FCSTD DOCUMENT  (FreeCAD 1.0R39319 (Git))
Label: ASSEMBLY-TEK2-PCB
License: All rights reserved
LicenseURL: https://en.wikipedia.org/wiki/All_rights_reserved
objects: App::Link×21, Part::FeaturePython×7, App::DocumentObjectGroup×3, PartDesign::CoordinateSystem×1, App::FeaturePython×1, App::Part×1
note: 8 computed .brp shape members not serialized (recipe doc carries the construction recipe); baked Part::Feature solids carry a one-line shape summary decoded from their .brp
EXTERNAL_REF file=PCBAs/PCBA-VSNX.FCStd obj=LCS_1
EXTERNAL_REF file=PCBAs/PCBA-VSNX.FCStd obj=PCBA_VSNX_3D_1
EXTERNAL_REF file=PCBAs/PCBA-VSNX.FCStd obj=Plane_2
EXTERNAL_REF file=PCBAs/PCBA-VSNX-SPACER.FCStd obj=Plane_Bottom_1
EXTERNAL_REF file=PCBAs/PCBA-VSNX-SPACER.FCStd obj=PCBA_VSNX_SPACER_3D_1
EXTERNAL_REF file=PCBAs/PCBA-VSNX-SPACER.FCStd obj=Plane_Top_1
EXTERNAL_REF file=PCBAs/PCBA-VSNX-LCDMOUNT-LEFT.FCStd obj=Plane_1
EXTERNAL_REF file=PCBAs/PCBA-VSNX-LCDMOUNT-TEK2.FCStd obj=PCBA_VSNX_LCDMOUNT_3D_1
EXTERNAL_REF file=PCBAs/PCBA-VSNX.FCStd obj=Axis_3
EXTERNAL_REF file=../Design/THT-ENDLESSPOT/THT-ENDLESSPOT.FCStd obj=Axis_1
EXTERNAL_REF file=../Design/THT-ENDLESSPOT/THT-ENDLESSPOT.FCStd obj=Body
EXTERNAL_REF file=PCBAs/PCBA-VSNX-LCDMOUNT-LEFT.FCStd obj=CircleAxis_1
EXTERNAL_REF file=../Design/SCREW-M1.6x5-C/SCREW-M1.6x5-C.FCStd obj=CircleAxis_1
EXTERNAL_REF file=../Design/SCREW-M1.6x5-C/SCREW-M1.6x5-C.FCStd obj=Body
EXTERNAL_REF file=PCBAs/PCBA-VSNX-LCDMOUNT-LEFT.FCStd obj=CircleAxis_2
EXTERNAL_REF file=PCBAs/PCBA-VSNX-LCDMOUNT-LEFT.FCStd obj=CircleAxis_3
EXTERNAL_REF file=PCBAs/PCBA-VSNX-LCDMOUNT-LEFT.FCStd obj=CircleAxis_4
EXTERNAL_REF file=PCBAs/PCBA-VSNX-LCDMOUNT-LEFT.FCStd obj=CircleAxis_5
EXTERNAL_REF file=PCBAs/PCBA-VSNX-LCDMOUNT-LEFT.FCStd obj=CircleAxis_6
EXTERNAL_REF file=PCBAs/PCBA-VSNX-LCDMOUNT-LEFT.FCStd obj=CircleAxis_7
EXTERNAL_REF file=PCBAs/PCBA-VSNX-LCDMOUNT-LEFT.FCStd obj=CircleAxis_8
EXTERNAL_REF file=PCBAs/PCBA-VSNX-LCDMOUNT-LEFT.FCStd obj=LCS_2
EXTERNAL_REF file=../Design/THT-HALL-SWITCH/THT-HALL-SWITCH.FCStd obj=LCS_Origin
EXTERNAL_REF file=../Design/THT-HALL-SWITCH/THT-HALL-SWITCH.FCStd obj=Body
EXTERNAL_REF file=../Design/PLASTIC-LOW-PROFILE-KEYCAP/PLASTIC-LOW-PROFILE-KEYCAP_THT.FCStd obj=LCS_1
EXTERNAL_REF file=../Design/THT-HALL-SWITCH/THT-HALL-SWITCH.FCStd obj=LCS_1
EXTERNAL_REF file=../Design/PLASTIC-LOW-PROFILE-KEYCAP/PLASTIC-LOW-PROFILE-KEYCAP_THT.FCStd obj=Body
EXTERNAL_REF file=PCBAs/PCBA-VSNX.FCStd obj=LCS_3
EXTERNAL_REF file=../Design/SPACER/SPACER.FCStd obj=LCS_1
EXTERNAL_REF file=../Design/SPACER/SPACER.FCStd obj=Body004
EXTERNAL_REF file=PCBAs/PCBA-VSNX.FCStd obj=LCS_4
EXTERNAL_REF file=../Design/SCREW-M1.6x8/SCREW-M1.6x8.FCStd obj=LCS_1
EXTERNAL_REF file=../Design/SPACER/SPACER.FCStd obj=LCS_2
EXTERNAL_REF file=../Design/SCREW-M1.6x8/SCREW-M1.6x8.FCStd obj=Body
EXTERNAL_REF file=../Design/PLASTIC-TEK2-KNOB-INTERFACE/PLASTIC-TEK2-KNOB-INTERFACE.FCStd obj=LCS_2
EXTERNAL_REF file=../Design/THT-ENDLESSPOT/THT-ENDLESSPOT.FCStd obj=LCS_2
EXTERNAL_REF file=../Design/PLASTIC-TEK2-KNOB-INTERFACE/PLASTIC-TEK2-KNOB-INTERFACE.FCStd obj=Body
EXTERNAL_REF file=../Design/KNOB-TEK2/KNOB-TEK2.FCStd obj=LCS_1
EXTERNAL_REF file=../Design/PLASTIC-TEK2-KNOB-INTERFACE/PLASTIC-TEK2-KNOB-INTERFACE.FCStd obj=LCS_1
EXTERNAL_REF file=../Design/KNOB-TEK2/KNOB-TEK2.FCStd obj=Body

FEATURE [App::DocumentObjectGroup] Parts
FEATURE [PartDesign::CoordinateSystem] LCS_Origin
  AttacherType = Attacher::AttachEngine3D
  AttachmentSupport = -> [X_Axis]
  MapMode = 2
FEATURE [App::DocumentObjectGroup] Constraints
FEATURE [App::FeaturePython] Variables  # WARN: FeaturePython — macro-defined, semantics opaque (R4)
  Type = App::PropertyContainer
FEATURE [App::DocumentObjectGroup] Configurations
FEATURE [App::Link] PCBA_VSNX_3D_1  label="PCBA-VSNX-3D 1"
  AttachedBy = #LCS_1
  AttachedTo = Parent Assembly#LCS_Origin
  LinkedObject = -> <external PCBAs/PCBA-VSNX.FCStd>#PCBA_VSNX_3D_1
  SolverId = Asm4EE
  expr: Placement = LCS_Origin.Placement * AttachmentOffset * PCBA_VSNX#LCS_1.Placement ^ -1
FEATURE [App::Link] PCBA_VSNX_SPACER_3D_1  label="PCBA-VSNX-SPACER-3D 1"
  AttachedBy = #Plane_Bottom_1
  AttachedTo = PCBA_VSNX_3D_1#Plane_2
  AttachmentOffset = pos=(0,0,0) rot=(1,0,0;3.14159rad)
  LinkPlacement = pos=(0,0,1.51) rot=(0,0,1;0rad)
  LinkedObject = -> <external PCBAs/PCBA-VSNX-SPACER.FCStd>#PCBA_VSNX_SPACER_3D_1
  Placement = pos=(0,0,1.51) rot=(0,0,1;0rad)
  SolverId = Asm4EE
  expr: Placement = PCBA_VSNX_3D_1.Placement * PCBA_VSNX#Plane_2.Placement * AttachmentOffset * PCBA_VSNX_SPACER#Plane_Bottom_1.Placement ^ -1
FEATURE [App::Link] PCBA_VSNX_SPACER_3D_002  label="PCBA-VSNX-SPACER-3D 002"
  AttachedBy = #Plane_Bottom_1
  AttachedTo = PCBA_VSNX_SPACER_3D_1#Plane_Top_1
  AttachmentOffset = pos=(0,0,0) rot=(1,0,0;3.14159rad)
  LinkPlacement = pos=(0,0,2.62) rot=(0,0,1;0rad)
  LinkedObject = -> <external PCBAs/PCBA-VSNX-SPACER.FCStd>#PCBA_VSNX_SPACER_3D_1
  Placement = pos=(0,0,2.62) rot=(0,0,1;0rad)
  SolverId = Asm4EE
  expr: Placement = PCBA_VSNX_SPACER_3D_1.Placement * PCBA_VSNX_SPACER#Plane_Top_1.Placement * AttachmentOffset * PCBA_VSNX_SPACER#Plane_Bottom_1.Placement ^ -1
FEATURE [App::Link] PCBA_VSNX_LCDMOUNT_3D_1  label="PCBA-VSNX-LCDMOUNT-3D 1"
  AttachedBy = #Plane_1
  AttachedTo = PCBA_VSNX_SPACER_3D_002#Plane_Top_1
  AttachmentOffset = pos=(0,0,0) rot=(1,0,0;3.14159rad)
  LinkPlacement = pos=(0,0,3.73) rot=(0,0,1;0rad)
  LinkedObject = -> <external PCBAs/PCBA-VSNX-LCDMOUNT-TEK2.FCStd>#PCBA_VSNX_LCDMOUNT_3D_1
  Placement = pos=(0,0,3.73) rot=(0,0,1;0rad)
  SolverId = Asm4EE
  expr: Placement = PCBA_VSNX_SPACER_3D_002.Placement * PCBA_VSNX_SPACER#Plane_Top_1.Placement * AttachmentOffset * PCBA_VSNX_LCDMOUNT_LEFT#Plane_1.Placement ^ -1
FEATURE [App::Link] THT_ENDLESSPOT  label="THT-ENDLESSPOT"
  AttachedBy = #Axis_1
  AttachedTo = PCBA_VSNX_3D_1#Axis_3
  AttachmentOffset = pos=(0,0,-25) rot=(0,-1,0;3.14159rad)
  LinkPlacement = pos=(26.6653,26.6675,1.50877) rot=(0,0,1;4.71239rad)
  LinkedObject = -> <external ../Design/THT-ENDLESSPOT/THT-ENDLESSPOT.FCStd>#Body
  Placement = pos=(26.6653,26.6675,1.50877) rot=(0,0,1;4.71239rad)
  SolverId = Asm4EE
  expr: Placement = PCBA_VSNX_3D_1.Placement * PCBA_VSNX#Axis_3.Placement * AttachmentOffset * THT_ENDLESSPOT#Axis_1.Placement ^ -1
FEATURE [App::Link] SCREW_M1_6x5_C  label="SCREW-M1.6x5-C"
  AttachedBy = #CircleAxis_1
  AttachedTo = PCBA_VSNX_LCDMOUNT_3D_1#CircleAxis_1
  AttachmentOffset = pos=(0,0,0) rot=(1,0,0;3.14159rad)
  LinkPlacement = pos=(-25.8762,-12.9381,4.04) rot=(0,0,1;1.5708rad)
  LinkedObject = -> <external ../Design/SCREW-M1.6x5-C/SCREW-M1.6x5-C.FCStd>#Body
  Placement = pos=(-25.8762,-12.9381,4.04) rot=(0,0,1;1.5708rad)
  SolverId = Asm4EE
  expr: Placement = PCBA_VSNX_LCDMOUNT_3D_1.Placement * PCBA_VSNX_LCDMOUNT_LEFT#CircleAxis_1.Placement * AttachmentOffset * SCREW_M1_6x5_C#CircleAxis_1.Placement ^ -1
FEATURE [App::Link] SCREW_M1_6x5_C001  label="SCREW-M1.6x5-C001"
  AttachedBy = #CircleAxis_1
  AttachedTo = PCBA_VSNX_LCDMOUNT_3D_1#CircleAxis_2
  AttachmentOffset = pos=(0,0,0) rot=(1,0,0;3.14159rad)
  LinkPlacement = pos=(-25.8762,-38.8144,4.04) rot=(0,0,1;1.5708rad)
  LinkedObject = -> <external ../Design/SCREW-M1.6x5-C/SCREW-M1.6x5-C.FCStd>#Body
  Placement = pos=(-25.8762,-38.8144,4.04) rot=(0,0,1;1.5708rad)
  SolverId = Asm4EE
  expr: Placement = PCBA_VSNX_LCDMOUNT_3D_1.Placement * PCBA_VSNX_LCDMOUNT_LEFT#CircleAxis_2.Placement * AttachmentOffset * SCREW_M1_6x5_C#CircleAxis_1.Placement ^ -1
FEATURE [App::Link] SCREW_M1_6x5_C002  label="SCREW-M1.6x5-C002"
  AttachedBy = #CircleAxis_1
  AttachedTo = PCBA_VSNX_LCDMOUNT_3D_1#CircleAxis_3
  AttachmentOffset = pos=(0,0,0) rot=(1,0,0;3.14159rad)
  LinkPlacement = pos=(25.8762,-12.9381,4.04) rot=(0,0,1;1.5708rad)
  LinkedObject = -> <external ../Design/SCREW-M1.6x5-C/SCREW-M1.6x5-C.FCStd>#Body
  Placement = pos=(25.8762,-12.9381,4.04) rot=(0,0,1;1.5708rad)
  SolverId = Asm4EE
  expr: Placement = PCBA_VSNX_LCDMOUNT_3D_1.Placement * PCBA_VSNX_LCDMOUNT_LEFT#CircleAxis_3.Placement * AttachmentOffset * SCREW_M1_6x5_C#CircleAxis_1.Placement ^ -1
FEATURE [App::Link] SCREW_M1_6x5_C003  label="SCREW-M1.6x5-C003"
  AttachedBy = #CircleAxis_1
  AttachedTo = PCBA_VSNX_LCDMOUNT_3D_1#CircleAxis_4
  AttachmentOffset = pos=(0,0,0) rot=(1,0,0;3.14159rad)
  LinkPlacement = pos=(25.8762,-38.8144,4.04) rot=(0,0,1;1.5708rad)
  LinkedObject = -> <external ../Design/SCREW-M1.6x5-C/SCREW-M1.6x5-C.FCStd>#Body
  Placement = pos=(25.8762,-38.8144,4.04) rot=(0,0,1;1.5708rad)
  SolverId = Asm4EE
  expr: Placement = PCBA_VSNX_LCDMOUNT_3D_1.Placement * PCBA_VSNX_LCDMOUNT_LEFT#CircleAxis_4.Placement * AttachmentOffset * SCREW_M1_6x5_C#CircleAxis_1.Placement ^ -1
FEATURE [App::Link] SCREW_M1_6x5_C004  label="SCREW-M1.6x5-C004"
  AttachedBy = #CircleAxis_1
  AttachedTo = PCBA_VSNX_LCDMOUNT_3D_1#CircleAxis_5
  AttachmentOffset = pos=(0,0,0) rot=(1,0,0;3.14159rad)
  LinkPlacement = pos=(38.17,36.67,4.04) rot=(0,0,1;1.5708rad)
  LinkedObject = -> <external ../Design/SCREW-M1.6x5-C/SCREW-M1.6x5-C.FCStd>#Body
  Placement = pos=(38.17,36.67,4.04) rot=(0,0,1;1.5708rad)
  SolverId = Asm4EE
  expr: Placement = PCBA_VSNX_LCDMOUNT_3D_1.Placement * PCBA_VSNX_LCDMOUNT_LEFT#CircleAxis_5.Placement * AttachmentOffset * SCREW_M1_6x5_C#CircleAxis_1.Placement ^ -1
FEATURE [App::Link] SCREW_M1_6x5_C005  label="SCREW-M1.6x5-C005"
  AttachedBy = #CircleAxis_1
  AttachedTo = PCBA_VSNX_LCDMOUNT_3D_1#CircleAxis_6
  AttachmentOffset = pos=(0,0,0) rot=(1,0,0;3.14159rad)
  LinkPlacement = pos=(38.17,16.67,4.04) rot=(0,0,1;1.5708rad)
  LinkedObject = -> <external ../Design/SCREW-M1.6x5-C/SCREW-M1.6x5-C.FCStd>#Body
  Placement = pos=(38.17,16.67,4.04) rot=(0,0,1;1.5708rad)
  SolverId = Asm4EE
  expr: Placement = PCBA_VSNX_LCDMOUNT_3D_1.Placement * PCBA_VSNX_LCDMOUNT_LEFT#CircleAxis_6.Placement * AttachmentOffset * SCREW_M1_6x5_C#CircleAxis_1.Placement ^ -1
FEATURE [App::Link] SCREW_M1_6x5_C006  label="SCREW-M1.6x5-C006"
  AttachedBy = #CircleAxis_1
  AttachedTo = PCBA_VSNX_LCDMOUNT_3D_1#CircleAxis_7
  AttachmentOffset = pos=(0,0,0) rot=(1,0,0;3.14159rad)
  LinkPlacement = pos=(-38.17,16.67,4.04) rot=(0,0,1;1.5708rad)
  LinkedObject = -> <external ../Design/SCREW-M1.6x5-C/SCREW-M1.6x5-C.FCStd>#Body
  Placement = pos=(-38.17,16.67,4.04) rot=(0,0,1;1.5708rad)
  SolverId = Asm4EE
  expr: Placement = PCBA_VSNX_LCDMOUNT_3D_1.Placement * PCBA_VSNX_LCDMOUNT_LEFT#CircleAxis_7.Placement * AttachmentOffset * SCREW_M1_6x5_C#CircleAxis_1.Placement ^ -1
FEATURE [App::Link] SCREW_M1_6x5_C007  label="SCREW-M1.6x5-C007"
  AttachedBy = #CircleAxis_1
  AttachedTo = PCBA_VSNX_LCDMOUNT_3D_1#CircleAxis_8
  AttachmentOffset = pos=(0,0,0) rot=(1,0,0;3.14159rad)
  LinkPlacement = pos=(-38.17,36.67,4.04) rot=(0,0,1;1.5708rad)
  LinkedObject = -> <external ../Design/SCREW-M1.6x5-C/SCREW-M1.6x5-C.FCStd>#Body
  Placement = pos=(-38.17,36.67,4.04) rot=(0,0,1;1.5708rad)
  SolverId = Asm4EE
  expr: Placement = PCBA_VSNX_LCDMOUNT_3D_1.Placement * PCBA_VSNX_LCDMOUNT_LEFT#CircleAxis_8.Placement * AttachmentOffset * SCREW_M1_6x5_C#CircleAxis_1.Placement ^ -1
FEATURE [App::Link] Body  label="THT-HALL-SWITCH"
  AttachedBy = #LCS_Origin
  AttachedTo = PCBA_VSNX_LCDMOUNT_3D_1#LCS_2
  LinkPlacement = pos=(-25.5144,-43.3144,3.74) rot=(0,0,1;0rad)
  LinkedObject = -> <external ../Design/THT-HALL-SWITCH/THT-HALL-SWITCH.FCStd>#Body
  Placement = pos=(-25.5144,-43.3144,3.74) rot=(0,0,1;0rad)
  SolverId = Asm4EE
  expr: Placement = PCBA_VSNX_LCDMOUNT_3D_1.Placement * PCBA_VSNX_LCDMOUNT_LEFT#LCS_2.Placement * AttachmentOffset * THT_HALL_SWITCH#LCS_Origin.Placement ^ -1
FEATURE [Part::FeaturePython] Linear_Body  label="Linear_THT-HALL-SWITCH"  # Draft array (typed FeaturePython)
  ArrayType = Linear Array
  Axis = -> LCS_Origin [X]
  AxisPlacement = pos=(0,0,0) rot=(0.57735,0.57735,0.57735;2.0944rad)
  Count = 4
  Index = 1
  LinearStep = 25.88
  PlacementList = 4 placements: arithmetic series from (-25.5144,-43.3144,3.74) step (25.88,0,2.66454e-15) to (52.1256,-43.3144,3.74)
  Placer = pos=(0,0,77.64) rot=(0,0,1;0rad)
  ScaleList = (4) [(1,1,1),(1,1,1),(1,1,1),(1,1,1)]
  Scaler = 1
  ShowElement = false
  SourceObject = -> Body
  expr: .Placer.Base.z = LinearStep * Index
FEATURE [Part::FeaturePython] Linear_Linear_Body  label="Linear_Linear_THT-HALL-SWITCH"  # Draft array (typed FeaturePython)
  ArrayType = Linear Array
  Axis = -> LCS_Origin [Y]
  AxisPlacement = pos=(0,0,0) rot=(0.57735,0.57735,0.57735;4.18879rad)
  Count = 2
  Index = 1
  LinearStep = 25.88
  PlacementList = 2 placements: [(0,0,0),(8.61977e-15,25.88,-8.61977e-15)]
  Placer = pos=(0,0,25.88) rot=(0,0,1;0rad)
  ScaleList = (2) [(1,1,1),(1,1,1)]
  Scaler = 1
  ShowElement = false
  SourceObject = -> Linear_Body
  expr: .Placer.Base.z = LinearStep * Index
FEATURE [App::Link] PLASTIC_LOW_PROFILE_KEYCAP  label="PLASTIC-LOW-PROFILE-KEYCAP"
  AttachedBy = #LCS_1
  AttachedTo = Body#LCS_1
  AttachmentOffset = pos=(0,0,0) rot=(0,0,1;1.5708rad)
  LinkPlacement = pos=(-38.8144,-38.8144,10.0402) rot=(0,0,-1;3.14159rad)
  LinkedObject = -> <external ../Design/PLASTIC-LOW-PROFILE-KEYCAP/PLASTIC-LOW-PROFILE-KEYCAP_THT.FCStd>#Body
  Placement = pos=(-38.8144,-38.8144,10.0402) rot=(0,0,-1;3.14159rad)
  SolverId = Asm4EE
  expr: Placement = Body.Placement * THT_HALL_SWITCH#LCS_1.Placement * AttachmentOffset * PLASTIC_LOW_PROFILE_KEYCAP_THT#LCS_1.Placement ^ -1
FEATURE [Part::FeaturePython] Linear_PLASTIC_LOW_PROFILE_KEYCAP  label="Linear_PLASTIC-LOW-PROFILE-KEYCAP"  # Draft array (typed FeaturePython)
  ArrayType = Linear Array
  Axis = -> LCS_Origin [X]
  AxisPlacement = pos=(0,0,0) rot=(0.57735,0.57735,0.57735;2.0944rad)
  Count = 4
  Index = 1
  LinearStep = 25.88
  PlacementList = 4 placements: arithmetic series from (-38.8144,-38.8144,10.0402) step (25.88,0,3.55271e-15) to (38.8256,-38.8144,10.0402)
  Placer = pos=(0,0,77.64) rot=(0,0,1;0rad)
  ScaleList = (4) [(1,1,1),(1,1,1),(1,1,1),(1,1,1)]
  Scaler = 1
  ShowElement = false
  SourceObject = -> PLASTIC_LOW_PROFILE_KEYCAP
  expr: .Placer.Base.z = LinearStep * Index
FEATURE [Part::FeaturePython] Linear_Linear_PLASTIC_LOW_PROFILE_KEYCAP  label="Linear_Linear_PLASTIC-LOW-PROFILE-KEYCAP"  # Draft array (typed FeaturePython)
  ArrayType = Linear Array
  Axis = -> LCS_Origin [Y]
  AxisPlacement = pos=(0,0,0) rot=(0.57735,0.57735,0.57735;4.18879rad)
  Count = 2
  Index = 1
  LinearStep = 25.88
  PlacementList = 2 placements: [(0,0,0),(8.61977e-15,25.88,-8.61977e-15)]
  Placer = pos=(0,0,25.88) rot=(0,0,1;0rad)
  ScaleList = (2) [(1,1,1),(1,1,1)]
  Scaler = 1
  ShowElement = false
  SourceObject = -> Linear_PLASTIC_LOW_PROFILE_KEYCAP
  expr: .Placer.Base.z = LinearStep * Index
FEATURE [App::Link] SPACER
  AttachedBy = #LCS_1
  AttachedTo = PCBA_VSNX_3D_1#LCS_3
  AttachmentOffset = pos=(0,0,0) rot=(1,0,0;3.14159rad)
  LinkPlacement = pos=(-26.67,-26.67,1.51) rot=(0,0,-1;3.14159rad)
  LinkedObject = -> <external ../Design/SPACER/SPACER.FCStd>#Body004
  Placement = pos=(-26.67,-26.67,1.51) rot=(0,0,-1;3.14159rad)
  SolverId = Asm4EE
  expr: Placement = PCBA_VSNX_3D_1.Placement * PCBA_VSNX#LCS_3.Placement * AttachmentOffset * SPACER#LCS_1.Placement ^ -1
FEATURE [App::Link] SPACER001
  AttachedBy = #LCS_1
  AttachedTo = PCBA_VSNX_3D_1#LCS_4
  AttachmentOffset = pos=(0,0,0) rot=(1,0,0;3.14159rad)
  LinkPlacement = pos=(26.67,-26.67,1.51) rot=(0,0,-1;3.14159rad)
  LinkedObject = -> <external ../Design/SPACER/SPACER.FCStd>#Body004
  Placement = pos=(26.67,-26.67,1.51) rot=(0,0,-1;3.14159rad)
  SolverId = Asm4EE
  expr: Placement = PCBA_VSNX_3D_1.Placement * PCBA_VSNX#LCS_4.Placement * AttachmentOffset * SPACER#LCS_1.Placement ^ -1
FEATURE [App::Link] SCREW_M1_6x8  label="SCREW-M1.6x8"
  AttachedBy = #LCS_1
  AttachedTo = SPACER#LCS_2
  LinkPlacement = pos=(-26.67,-26.67,3.51) rot=(0,0,-1;3.14159rad)
  LinkedObject = -> <external ../Design/SCREW-M1.6x8/SCREW-M1.6x8.FCStd>#Body
  Placement = pos=(-26.67,-26.67,3.51) rot=(0,0,-1;3.14159rad)
  SolverId = Asm4EE
  expr: Placement = SPACER.Placement * SPACER#LCS_2.Placement * AttachmentOffset * SCREW_M1_6x8#LCS_1.Placement ^ -1
FEATURE [App::Link] SCREW_M1_6x009  label="SCREW-M1.6x009"
  AttachedBy = #LCS_1
  AttachedTo = SPACER001#LCS_2
  LinkPlacement = pos=(26.67,-26.67,3.51) rot=(0,0,-1;3.14159rad)
  LinkedObject = -> <external ../Design/SCREW-M1.6x8/SCREW-M1.6x8.FCStd>#Body
  Placement = pos=(26.67,-26.67,3.51) rot=(0,0,-1;3.14159rad)
  SolverId = Asm4EE
  expr: Placement = SPACER001.Placement * SPACER#LCS_2.Placement * AttachmentOffset * SCREW_M1_6x8#LCS_1.Placement ^ -1
FEATURE [App::Link] PLASTIC_TEK2_KNOB_INTERFACE  label="PLASTIC-TEK2-KNOB-INTERFACE"
  AttachedBy = #LCS_2
  AttachedTo = THT_ENDLESSPOT#LCS_2
  AttachmentOffset = pos=(0,0,0) rot=(-1,0,0;3.14159rad)
  LinkPlacement = pos=(26.67,26.67,22.06) rot=(0,0,1;4.71204rad)
  LinkedObject = -> <external ../Design/PLASTIC-TEK2-KNOB-INTERFACE/PLASTIC-TEK2-KNOB-INTERFACE.FCStd>#Body
  Placement = pos=(26.67,26.67,22.06) rot=(0,0,1;4.71204rad)
  SolverId = Asm4EE
  expr: Placement = THT_ENDLESSPOT.Placement * THT_ENDLESSPOT#LCS_2.Placement * AttachmentOffset * PLASTIC_TEK2_KNOB_INTERFACE#LCS_2.Placement ^ -1
FEATURE [App::Link] KNOB_TEK2  label="KNOB-TEK2"
  AttachedBy = #LCS_1
  AttachedTo = PLASTIC_TEK2_KNOB_INTERFACE#LCS_1
  AttachmentOffset = pos=(0,0,0) rot=(0,0,1;3.14159rad)
  LinkPlacement = pos=(27.4105,26.6719,12.81) rot=(0,0,-1;4.70988rad)
  LinkedObject = -> <external ../Design/KNOB-TEK2/KNOB-TEK2.FCStd>#Body
  Placement = pos=(27.4105,26.6719,12.81) rot=(0,0,-1;4.70988rad)
  SolverId = Asm4EE
  expr: Placement = PLASTIC_TEK2_KNOB_INTERFACE.Placement * PLASTIC_TEK2_KNOB_INTERFACE#LCS_1.Placement * AttachmentOffset * KNOB_TEK2#LCS_1.Placement ^ -1
FEATURE [Part::FeaturePython] Mirror_THT_ENDLESSPOT  label="Mirror_THT-ENDLESSPOT"  # Draft array (typed FeaturePython)
  ArrayType = Mirror Array
  Axis = -> LCS_Origin [X]
  AxisPlacement = pos=(0,0,0) rot=(0.57735,0.57735,0.57735;2.0944rad)
  Count = 2
  Index = 1
  PlacementList = 2 placements: [(26.6653,26.6675,1.50877),(-26.6653,26.6675,1.50877)]
  Placer = pos=(53.3349,3.01755,-53.3307) rot=(0,0,1;3.14159rad)
  ScaleList = (2) [(1,1,1),(-1,-1,-1)]
  Scaler = -1
  ShowElement = false
  SourceObject = -> THT_ENDLESSPOT
  expr: .Placer.Base = .Placer.Rotation * minvert(.AxisPlacement) * .SourceObject.Placement.Base * -2 * (Index % 2)
  expr: .Placer.Rotation.Angle = 180 * (Index % 2)
  expr: Scaler = 1 - 2 * (Index % 2)
FEATURE [Part::FeaturePython] Mirror_PLASTIC_TEK2_KNOB_INTERFACE  label="Mirror_PLASTIC-TEK2-KNOB-INTERFACE"  # Draft array (typed FeaturePython)
  ArrayType = Mirror Array
  Axis = -> LCS_Origin [X]
  AxisPlacement = pos=(0,0,0) rot=(0.57735,0.57735,0.57735;2.0944rad)
  Count = 2
  Index = 1
  PlacementList = 2 placements: [(26.67,26.67,22.06),(-26.67,26.67,22.06)]
  Placer = pos=(53.34,44.12,-53.34) rot=(0,0,1;3.14159rad)
  ScaleList = (2) [(1,1,1),(-1,-1,-1)]
  Scaler = -1
  ShowElement = false
  SourceObject = -> PLASTIC_TEK2_KNOB_INTERFACE
  expr: .Placer.Base = .Placer.Rotation * minvert(.AxisPlacement) * .SourceObject.Placement.Base * -2 * (Index % 2)
  expr: .Placer.Rotation.Angle = 180 * (Index % 2)
  expr: Scaler = 1 - 2 * (Index % 2)
FEATURE [Part::FeaturePython] Mirror_KNOB_TEK2  label="Mirror_KNOB-TEK2"  # Draft array (typed FeaturePython)
  ArrayType = Mirror Array
  Axis = -> LCS_Origin [X]
  AxisPlacement = pos=(0,0,0) rot=(0.57735,0.57735,0.57735;2.0944rad)
  Count = 2
  Index = 1
  PlacementList = 2 placements: [(27.4105,26.6719,12.81),(-27.4105,26.6719,12.81)]
  Placer = pos=(53.3437,25.62,-54.821) rot=(0,0,1;3.14159rad)
  ScaleList = (2) [(1,1,1),(-1,-1,-1)]
  Scaler = -1
  ShowElement = false
  SourceObject = -> KNOB_TEK2
  expr: .Placer.Base = .Placer.Rotation * minvert(.AxisPlacement) * .SourceObject.Placement.Base * -2 * (Index % 2)
  expr: .Placer.Rotation.Angle = 180 * (Index % 2)
  expr: Scaler = 1 - 2 * (Index % 2)
FEATURE [App::Part] Assembly
  AssemblyType = Part::Link
  Group = -> [LCS_Origin,Constraints,Variables,Configurations,PCBA_VSNX_3D_1,PCBA_VSNX_SPACER_3D_1,PCBA_VSNX_SPACER_3D_002,PCBA_VSNX_LCDMOUNT_3D_1,THT_ENDLESSPOT,SCREW_M1_6x5_C,SCREW_M1_6x5_C001,SCREW_M1_6x5_C002,SCREW_M1_6x5_C003,SCREW_M1_6x5_C004,SCREW_M1_6x5_C005,SCREW_M1_6x5_C006,SCREW_M1_6x5_C007,Body,Linear_Body,Linear_Linear_Body,PLASTIC_LOW_PROFILE_KEYCAP,Linear_PLASTIC_LOW_PROFILE_KEYCAP,+10 more]
  Origin = -> Origin
  Type = Assembly

RESOLVED EXTERNAL PARTS (link-assembly join: the EXTERNAL_REF files above that resolve inside this repo's crawl, each included once):
---- part ../Design/KNOB-TEK2/KNOB-TEK2.FCStd = doc fcstd_0a6eb00ad0a5 ----
FCSTD DOCUMENT  (FreeCAD 1.0R39319 (Git))
Label: KNOB-TEK2
License: All rights reserved
LicenseURL: https://en.wikipedia.org/wiki/All_rights_reserved
objects: TechDraw::DrawViewDimension×14, Sketcher::SketchObject×7, TechDraw::DrawViewPart×5, TechDraw::DrawHatch×5, TechDraw::DrawViewBalloon×4, TechDraw::DrawViewAnnotation×2, PartDesign::Pocket×2, PartDesign::CoordinateSystem×2, Part::Feature×1, PartDesign::Plane×1, PartDesign::Pad×1, PartDesign::Boolean×1, TechDraw::DrawSVGTemplate×1, PartDesign::Fillet×1, PartDesign::Body×1, TechDraw::DrawComplexSection×1, TechDraw::DrawViewDimExtent×1, TechDraw::DrawPage×1
note: 58 computed .brp shape members not serialized (recipe doc carries the construction recipe); baked Part::Feature solids carry a one-line shape summary decoded from their .brp

FEATURE [Part::Feature] Part__Feature  label="alu_potmeter_002_04"
  shape: bbox 38.3 x 38.3 x 17.53 mm, 68 faces (baked)
FEATURE [PartDesign::Plane] DatumPlane
  AttachmentOffset = pos=(0,0,4.5) rot=(0,0,1;0rad)
  AttachmentSupport = -> [XY_Plane]
  Length = 60
  MapMode = 5
  Placement = pos=(0,0,4.5) rot=(0,0,1;0rad)
  ResizeMode = 0
  Width = 60
FEATURE [Sketcher::SketchObject] Sketch
  ArcFitTolerance = 0
  AttachmentSupport = -> [XY_Plane]
  FullyConstrained = true
  MakeInternals = false
  MapMode = 2
  sketch-geometry (1):
    g0: Circle CenterX=0 CenterY=0 CenterZ=0 NormalX=0 NormalY=0 NormalZ=1 AngleXU=0 Radius=15
  constraints (2):
    c: Coincident(g0,g-1)
    c: Diameter(g0) = 30
FEATURE [PartDesign::Pad] Pad
  Direction = (0,0,1)
  Length = 15
  Length2 = 10
  Profile = -> Sketch
  ReferenceAxis = -> Sketch [N_Axis]
  Refine = true
  Suppressed = false
  Type = 0
FEATURE [Sketcher::SketchObject] Sketch001
  ArcFitTolerance = 0
  AttachmentSupport = -> [DatumPlane]
  FullyConstrained = true
  MakeInternals = false
  MapMode = 5
  Placement = pos=(0,0,4.5) rot=(0,0,1;0rad)
  sketch-geometry (7):
    g0: ArcOfCircle CenterX=0 CenterY=0 CenterZ=0 NormalX=0 NormalY=0 NormalZ=1 AngleXU=0 Radius=7 StartAngle=5.63968 EndAngle=10.0683
    g1: LineSegment StartX=-4 StartY=-5 StartZ=0 EndX=4 EndY=-5 EndZ=0
    g2: Circle [constr] CenterX=0 CenterY=0 CenterZ=0 NormalX=0 NormalY=0 NormalZ=1 AngleXU=0 Radius=4.25
    g3: LineSegment [constr] StartX=0 StartY=-4.25 StartZ=0 EndX=0 EndY=-5 EndZ=0
    g4: ArcOfCircle CenterX=-4 CenterY=-3 CenterZ=0 NormalX=0 NormalY=0 NormalZ=1 AngleXU=0 Radius=2 StartAngle=3.78509 EndAngle=4.71239
    g5: ArcOfCircle CenterX=4 CenterY=-3 CenterZ=0 NormalX=0 NormalY=0 NormalZ=1 AngleXU=0 Radius=2 StartAngle=4.71239 EndAngle=5.63968
    g6: GeomPoint [constr] X=0 Y=7 Z=0
  constraints (20):
    c: Coincident(g0,g-1)
    c: Diameter(g0) = 14
    c: Horizontal(g1)
    c: Coincident(g2,g0)
    c: Diameter(g2) = 8.5
    c: PointOnObject(g3,g2)
    c: PointOnObject(g3,g1)
    c: Vertical(g3)
    c: PointOnObject(g3,g-2)
    c: DistanceY(g3,g3) = 0.75
    c: Tangent(g1,g4) = -1.5708
    c: Tangent(g0,g4) = -1.5708
    c: Tangent(g1,g5) = -1.5708
    c: Tangent(g0,g5) = -1.5708
    c: Equal(g5,g4)
    c: Diameter(g5) = 4
    c: DistanceY(g3,g0) = 5
    c: PointOnObject(g6,g0)
    c: PointOnObject(g6,g-2)
    c: DistanceY(g3,g6) = 12
FEATURE [PartDesign::Boolean] Boolean
  BaseFeature = -> Pad
  Group = -> [Part__Feature]
  Refine = true
  Suppressed = false
  Type = 0
  UsePlacement = false
FEATURE [TechDraw::DrawSVGTemplate] Template
  EditableTexts = COLOR=Sandblasted, black anodized (RAL code: 9004); CreationDate=2024/08/27; E.G.APPROVED=APPROVED; FC-Scale=2:1; FC-Title=KNOB-TEK2; IntechStudioLtd.=Intech Studio Ltd.; MATERIAL=Aluminum 6061-T6; REV=03; STANDARD=DIN 16742-TG5
  Height = 297
  Orientation = 1
  Template = <userpath>/Documents/grid-hardware/Manufacturing/FreeCAD_technical_drawing_template/A3_LandscapeTD_MODIFIED.svg
  Width = 420
FEATURE [Sketcher::SketchObject] Sketch002
  ArcFitTolerance = 0
  AttachmentSupport = -> [YZ_Plane]
  FullyConstrained = true
  MakeInternals = false
  MapMode = 5
  Placement = pos=(0,0,0) rot=(0.57735,0.57735,0.57735;2.0944rad)
  sketch-geometry (1):
    g0: LineSegment StartX=0 StartY=20 StartZ=0 EndX=0 EndY=-5 EndZ=0
  constraints (4):
    c: PointOnObject(g0,g-2)
    c: PointOnObject(g0,g-2)
    c: DistanceY(g0,g0) = 25
    c: DistanceY(g0,g-1) = 5
FEATURE [TechDraw::DrawViewAnnotation] Annotation
  Font = osifont
  LineSpace = 100
  LockPosition = false
  MaxWidth = -1
  Rotation = 0
  Scale = 2
  ScaleType = 0
  Text = Non-aesthetical side (purple): | No burrs
  TextSize = 5
  TextStyle = 0
  X = 278.355
  Y = 88.8334
FEATURE [Sketcher::SketchObject] Sketch004
  ArcFitTolerance = 0
  AttachmentSupport = -> [XY_Plane]
  FullyConstrained = true
  MakeInternals = false
  MapMode = 5
  sketch-geometry (1):
    g0: Circle CenterX=0 CenterY=0 CenterZ=0 NormalX=0 NormalY=0 NormalZ=1 AngleXU=0 Radius=10
  constraints (2):
    c: Coincident(g0,g-1)
    c: Diameter(g0) = 20
FEATURE [PartDesign::Pocket] Pocket001
  BaseFeature = -> Boolean
  Direction = (0,0,-1)
  Length = 4.5
  Length2 = 5
  Profile = -> Sketch004
  ReferenceAxis = -> Sketch004 [N_Axis]
  Refine = true
  Reversed = true
  Suppressed = false
  Type = 0
FEATURE [PartDesign::Pocket] Pocket
  BaseFeature = -> Pocket001
  Direction = (0,0,-1)
  Length = 9.5
  Length2 = 5
  Profile = -> Sketch001
  ReferenceAxis = -> Sketch001 [N_Axis]
  Refine = true
  Reversed = true
  Suppressed = false
  Type = 0
FEATURE [TechDraw::DrawViewAnnotation] Annotation001
  Font = osifont
  LineSpace = 100
  LockPosition = false
  MaxWidth = -1
  Rotation = 0
  Scale = 2
  ScaleType = 0
  Text = Section A-A
  TextSize = 4
  TextStyle = 0
  X = 199.631
  Y = 206.549
FEATURE [Sketcher::SketchObject] Sketch005
  ArcFitTolerance = 0
  AttachmentSupport = -> [DatumPlane]
  FullyConstrained = true
  MakeInternals = false
  MapMode = 5
  Placement = pos=(0,0,4.5) rot=(0,0,1;0rad)
  sketch-geometry (1):
    g0: Circle CenterX=0 CenterY=0 CenterZ=0 NormalX=0 NormalY=0 NormalZ=1 AngleXU=0 Radius=3.5
  constraints (2):
    c: Coincident(g0,g-1)
    c: Diameter(g0) = 7
FEATURE [PartDesign::Fillet] Fillet
  Base = -> Pocket [Edge136]
  BaseFeature = -> Pocket
  Radius = 1
  SupportTransform = false
  Suppressed = false
  UseAllEdges = false
FEATURE [Sketcher::SketchObject] Sketch006
  ArcFitTolerance = 0
  AttachmentSupport = -> [XY_Plane]
  FullyConstrained = true
  MakeInternals = false
  MapMode = 5
  sketch-geometry (5):
    g0: Circle CenterX=0 CenterY=0 CenterZ=0 NormalX=0 NormalY=0 NormalZ=1 AngleXU=0 Radius=6.975
    g1: Circle CenterX=0 CenterY=0 CenterZ=0 NormalX=0 NormalY=0 NormalZ=1 AngleXU=0 Radius=4.3
    g2: LineSegment StartX=-4.88876 StartY=4.975 StartZ=0 EndX=4.88876 EndY=4.975 EndZ=0
    g3: GeomPoint [constr] X=0 Y=-6.975 Z=0
    g4: GeomPoint [constr] X=0 Y=4.3 Z=0
  constraints (13):
    c: Coincident(g0,g-1)
    c: Coincident(g1,g0)
    c: PointOnObject(g2,g0)
    c: PointOnObject(g2,g0)
    c: Horizontal(g2)
    c: Diameter(g0) = 13.95
    c: Diameter(g1) = 8.6
    c: PointOnObject(g3,g0)
    c: PointOnObject(g3,g-2)
    c: DistanceY(g3,g2) = 11.95
    c: PointOnObject(g4,g1)
    c: DistanceY(g4,g2) = 0.675
    c: PointOnObject(g4,g-2)
FEATURE [Sketcher::SketchObject] Sketch007
  ArcFitTolerance = 0
  AttachmentSupport = -> [XY_Plane]
  FullyConstrained = true
  MakeInternals = false
  MapMode = 5
  sketch-geometry (4):
    g0: Circle CenterX=0 CenterY=0 CenterZ=0 NormalX=0 NormalY=0 NormalZ=1 AngleXU=0 Radius=0.1
    g1: Circle CenterX=0 CenterY=0.1 CenterZ=0 NormalX=0 NormalY=0 NormalZ=1 AngleXU=0 Radius=3.475
    g2: Circle CenterX=0 CenterY=-0.1 CenterZ=0 NormalX=0 NormalY=0 NormalZ=1 AngleXU=0 Radius=2.95
    g3: LineSegment StartX=0 StartY=-3.05 StartZ=0 EndX=0 EndY=-3.375 EndZ=0
  constraints (13):
    c: Coincident(g0,g-1)
    c: Diameter(g0) = 0.2
    c: PointOnObject(g1,g-2)
    c: PointOnObject(g1,g0)
    c: Diameter(g1) = 6.95
    c: PointOnObject(g2,g0)
    c: PointOnObject(g2,g-2)
    c: Diameter(g2) = 5.9
    c: PointOnObject(g3,g2)
    c: PointOnObject(g3,g1)
    c: Vertical(g3)
    c: PointOnObject(g3,g-2)
    c: DistanceY(g3,g3) = 0.325
FEATURE [PartDesign::CoordinateSystem] LCS_1
  AttacherType = Attacher::AttachEngine3D
  AttachmentSupport = -> [Fillet]
  MapMode = 45
  Placement = pos=(5e-16,0.740493,14) rot=(0,0,1;1.5708rad)
FEATURE [PartDesign::CoordinateSystem] LCS_2
  AttacherType = Attacher::AttachEngine3D
  AttachmentSupport = -> [Fillet]
  MapMode = 5
  Placement = pos=(0,0,14) rot=(1,0,0;3.14159rad)
FEATURE [PartDesign::Body] Body  label="KNOB-TEK2"
  AllowCompound = false
  Group = -> [DatumPlane,Sketch,Pad,Boolean,Pocket001,Sketch001,Pocket,Sketch002,Sketch004,Sketch005,Fillet,Sketch006,Sketch007,LCS_1,LCS_2]
  Origin = -> Origin
  Tip = -> Fillet
FEATURE [TechDraw::DrawViewPart] View
  CoarseView = false
  Direction = (-1,0,-3e-06)
  Focus = 100
  HardHidden = false
  IsoCount = 0
  IsoHidden = false
  IsoVisible = true
  LockPosition = false
  Perspective = false
  Rotation = 0
  Scale = 2
  ScaleType = 2
  ScrubCount = 0
  SeamHidden = false
  SeamVisible = true
  SmoothHidden = false
  SmoothVisible = true
  Source = -> [Body]
  X = 71.6241
  XDirection = (0,-1,0)
  Y = 240.603
FEATURE [TechDraw::DrawComplexSection] ComplexSection  label="Section A - A"
  BaseView = -> View
  CoarseView = false
  CutSurfaceDisplay = 3
  CuttingToolWireObject = -> Sketch002
  Direction = (0,1,-1e-16)
  FileGeomPattern = C:/Program Files/FreeCAD 0.21/data/Mod/TechDraw/PAT/FCPAT.pat
  FileHatchPattern = C:/Program Files/FreeCAD 0.21/data/Mod/TechDraw/Patterns/simple.svg
  Focus = 100
  FuseBeforeCut = false
  HardHidden = false
  HatchOffset = (0,0,0)
  HatchRotation = 0
  HatchScale = 1
  IsoCount = 0
  IsoHidden = false
  IsoVisible = true
  LockPosition = false
  NameGeomPattern = Gyémánt bevonatú
  Perspective = false
  ProjectionStrategy = 0
  Rotation = -90
  Scale = 2
  ScaleType = 0
  ScrubCount = 0
  SeamHidden = false
  SeamVisible = true
  SectionDirection = 4
  SectionLineStretch = 1
  SectionNormal = (0,1,-1e-16)
  SectionOrigin = (0,0,0)
  SectionSymbol = A
  SmoothHidden = false
  SmoothVisible = true
  Source = -> [Body]
  TrimAfterCut = false
  UsePreviousCut = false
  X = 199.631
  XDirection = (3e-06,-1e-16,-1)
  Y = 238.539
FEATURE [TechDraw::DrawViewPart] View001
  CoarseView = false
  Direction = (-3e-06,0,1)
  Focus = 100
  HardHidden = false
  IsoCount = 0
  IsoHidden = false
  IsoVisible = true
  LockPosition = false
  Perspective = false
  Rotation = 0
  Scale = 2
  ScaleType = 0
  ScrubCount = 0
  SeamHidden = false
  SeamVisible = true
  SmoothHidden = false
  SmoothVisible = true
  Source = -> [Body]
  X = 71.7073
  XDirection = (1,0,3e-06)
  Y = 150.924
FEATURE [TechDraw::DrawViewDimension] Dimension010
  AngleOverride = false
  Arbitrary = false
  ArbitraryTolerances = false
  EqualTolerance = true
  ExtensionAngle = 0
  FormatSpec = %.2w
  FormatSpecOverTolerance = %+.2w
  FormatSpecUnderTolerance = %+.2w
  Inverted = false
  LineAngle = 0
  LockPosition = false
  MeasureType = 1
  OverTolerance = 0
  References2D = -> [ComplexSection]
  Rotation = 0
  Scale = 2
  ScaleType = 0
  TheoreticalExact = false
  Type = 2
  UnderTolerance = 0
  X = 46.1971
  Y = -10.7931
FEATURE [TechDraw::DrawViewDimension] Dimension014
  AngleOverride = false
  Arbitrary = false
  ArbitraryTolerances = true
  EqualTolerance = false
  ExtensionAngle = 0
  FormatSpec = %.2w
  FormatSpecOverTolerance = +0
  FormatSpecUnderTolerance = -0.1
  Inverted = false
  LineAngle = 0
  LockPosition = false
  MeasureType = 1
  OverTolerance = 0
  References2D = -> [ComplexSection]
  Rotation = 0
  Scale = 2
  ScaleType = 0
  TheoreticalExact = false
  Type = 2
  UnderTolerance = 0
  X = 56.4159
  Y = 6.5209
FEATURE [TechDraw::DrawViewDimension] Dimension016
  AngleOverride = false
  Arbitrary = false
  ArbitraryTolerances = false
  EqualTolerance = true
  ExtensionAngle = 0
  FormatSpec = 12× %.2w
  FormatSpecOverTolerance = %+.2w
  FormatSpecUnderTolerance = %+.2w
  Inverted = false
  LineAngle = 0
  LockPosition = false
  MeasureType = 1
  OverTolerance = 0
  References2D = -> [View001]
  Rotation = 0
  Scale = 2
  ScaleType = 0
  TheoreticalExact = false
  Type = 2
  UnderTolerance = 0
  X = -56.7628
  Y = 0.276868
FEATURE [TechDraw::DrawViewPart] View002
  CoarseView = false
  Direction = (3e-06,1e-06,-1)
  Focus = 100
  HardHidden = false
  IsoCount = 0
  IsoHidden = false
  IsoVisible = true
  LockPosition = false
  Perspective = false
  Rotation = 0
  Scale = 2
  ScaleType = 0
  ScrubCount = 0
  SeamHidden = false
  SeamVisible = true
  SmoothHidden = false
  SmoothVisible = true
  Source = -> [Body]
  X = 200.492
  XDirection = (1,-3e-12,3e-06)
  Y = 152.25
FEATURE [TechDraw::DrawViewPart] View003
  CoarseView = false
  Direction = (-0.57735,0.57735,-0.57735)
  Focus = 100
  HardHidden = false
  IsoCount = 0
  IsoHidden = false
  IsoVisible = true
  LockPosition = false
  Perspective = false
  Rotation = 0
  Scale = 2
  ScaleType = 2
  ScrubCount = 0
  SeamHidden = false
  SeamVisible = true
  SmoothHidden = false
  SmoothVisible = true
  Source = -> [Body]
  X = 358.57
  XDirection = (-0.707102,-0.707111,-9.2376e-06)
  Y = 140.843
FEATURE [TechDraw::DrawViewPart] View004
  CoarseView = false
  Direction = (-0.57735,0.57735,0.57735)
  Focus = 100
  HardHidden = false
  IsoCount = 0
  IsoHidden = false
  IsoVisible = true
  LockPosition = false
  Perspective = false
  Rotation = 0
  Scale = 2
  ScaleType = 2
  ScrubCount = 0
  SeamHidden = false
  SeamVisible = true
  SmoothHidden = false
  SmoothVisible = true
  Source = -> [Body]
  X = 357.533
  XDirection = (-0.707111,-0.707101,-9.2376e-06)
  Y = 230.245
FEATURE [TechDraw::DrawHatch] Hatch  label="HatchF1"
  HatchPattern = C:/Program Files/FreeCAD 0.21/data/Mod/TechDraw/Patterns/solid.svg
  Source = -> View003 [Face1,Face44,Face15,Face7,Face3,Face19]
FEATURE [TechDraw::DrawHatch] Hatch001  label="Hatch001F13"
  HatchPattern = C:/Program Files/FreeCAD 0.21/data/Mod/TechDraw/Patterns/solid.svg
  Source = -> View004 [Face13,Face4,Face5,Face1,Face3,Face18,Face17,Face14,Face12,Face9,Face8,Face6,Face7,Face10,Face19,Face16,Face15,Face11,Face27,Face26,Face23,Face22,Face20,Face21,Face24,Face28,Face25]
FEATURE [TechDraw::DrawHatch] Hatch002  label="Hatch002F24"
  HatchPattern = C:/Program Files/FreeCAD 0.21/data/Mod/TechDraw/Patterns/solid.svg
  Source = -> View003 [Face24,Face25,Face28,Face29,Face32,Face33,Face36,Face37,Face38,Face35,Face34,Face31,Face30,Face27,Face26,Face23,Face22,Face20,Face21,Face11,Face8,Face6,Face4,Face5,Face9,Face10,Face13,Face17]
FEATURE [TechDraw::DrawViewBalloon] Balloon003
  BubbleShape = 1
  EndType = 3
  EndTypeScale = 1
  KinkLength = 0
  LockPosition = false
  OriginX = -14.9594
  OriginY = -6.7795
  Rotation = 0
  Scale = 2
  ScaleType = 0
  ShapeScale = 1
  SourceView = -> View003
  TextWrapLen = -1
  X = -29.1537
  Y = -19.8858
FEATURE [TechDraw::DrawViewDimension] Dimension027
  AngleOverride = false
  Arbitrary = false
  ArbitraryTolerances = false
  EqualTolerance = true
  ExtensionAngle = 0
  FormatSpec = ⌀%.2w
  FormatSpecOverTolerance = %+.2w
  FormatSpecUnderTolerance = %+.2w
  Inverted = false
  LineAngle = 0
  LockPosition = false
  MeasureType = 1
  OverTolerance = 0
  References2D = -> [View002]
  Rotation = 0
  Scale = 2
  ScaleType = 0
  TheoreticalExact = false
  Type = 5
  UnderTolerance = 0
  X = 58.2687
  Y = -4.50785
FEATURE [TechDraw::DrawViewDimExtent] DimExtent
  AngleOverride = false
  Arbitrary = false
  ArbitraryTolerances = false
  DirExtent = 0
  EqualTolerance = true
  ExtensionAngle = 0
  FormatSpec = ⌀%.2w
  FormatSpecOverTolerance = %+.2w
  FormatSpecUnderTolerance = %+.2w
  Inverted = false
  LineAngle = 0
  LockPosition = false
  MeasureType = 1
  OverTolerance = 0
  References2D = -> [View001]
  Rotation = 0
  Scale = 2
  ScaleType = 0
  Source = -> [View001]
  TheoreticalExact = false
  Type = 1
  UnderTolerance = 0
  X = -0.58901
  Y = -46.3131
FEATURE [TechDraw::DrawViewBalloon] Balloon
  BubbleShape = 6
  EndType = 6
  EndTypeScale = 1
  KinkLength = -0.1
  LockPosition = false
  OriginX = 19.3129
  OriginY = -26.049
  Rotation = 0
  Scale = 2
  ScaleType = 0
  ShapeScale = 1
  SourceView = -> DimExtent
  Text = A
  TextWrapLen = -1
  X = 24.4472
  Y = -26.0434
FEATURE [TechDraw::DrawViewDimension] Dimension029
  AngleOverride = false
  Arbitrary = false
  ArbitraryTolerances = false
  EqualTolerance = true
  ExtensionAngle = 0
  FormatSpec = ⌀%.2w
  FormatSpecOverTolerance = %+.2w
  FormatSpecUnderTolerance = %+.2w
  Inverted = false
  LineAngle = 0
  LockPosition = false
  MeasureType = 1
  OverTolerance = 0.05
  References2D = -> [ComplexSection]
  Rotation = 0
  Scale = 2
  ScaleType = 0
  TheoreticalExact = false
  Type = 1
  UnderTolerance = -0.05
  X = -51.7957
  Y = -20.9962
FEATURE [TechDraw::DrawViewBalloon] Balloon004
  BubbleShape = 6
  EndType = 6
  EndTypeScale = 1
  KinkLength = 0
  LockPosition = false
  OriginX = -30.2962
  OriginY = -14.1405
  Rotation = 0
  Scale = 2
  ScaleType = 0
  ShapeScale = 1
  SourceView = -> Dimension029
  Text = ◎|⌀ 0.2|A
  TextWrapLen = -1
  X = -22.8396
  Y = -16.0535
FEATURE [TechDraw::DrawViewDimension] Dimension030
  AngleOverride = false
  Arbitrary = false
  ArbitraryTolerances = false
  EqualTolerance = true
  ExtensionAngle = 0
  FormatSpec = R%.2w
  FormatSpecOverTolerance = %+.2w
  FormatSpecUnderTolerance = %+.2w
  Inverted = false
  LineAngle = 0
  LockPosition = false
  MeasureType = 1
  OverTolerance = 0
  References2D = -> [View002]
  Rotation = 0
  Scale = 2
  ScaleType = 0
  TheoreticalExact = false
  Type = 4
  UnderTolerance = 0
  X = 54.5926
  Y = 26.3888
FEATURE [TechDraw::DrawHatch] Hatch003  label="Hatch003F14"
  HatchPattern = C:/Program Files/FreeCAD 0.21/data/Mod/TechDraw/Patterns/solid.svg
  Source = -> View003 [Face14,Face16]
FEATURE [TechDraw::DrawHatch] Hatch004  label="Hatch004F18"
  HatchPattern = C:/Program Files/FreeCAD 0.21/data/Mod/TechDraw/Patterns/solid.svg
  Source = -> View003 [Face18,Face12]
FEATURE [TechDraw::DrawViewDimension] Dimension033
  AngleOverride = false
  Arbitrary = false
  ArbitraryTolerances = false
  EqualTolerance = true
  ExtensionAngle = 0
  FormatSpec = 12× %.2w
  FormatSpecOverTolerance = %+.2w
  FormatSpecUnderTolerance = %+.2w
  Inverted = false
  LineAngle = 0
  LockPosition = false
  MeasureType = 1
  OverTolerance = 0
  References2D = -> [View001]
  Rotation = 0
  Scale = 2
  ScaleType = 0
  TheoreticalExact = false
  Type = 2
  UnderTolerance = 0
  X = -46.3715
  Y = 0.067851
FEATURE [TechDraw::DrawViewDimension] Dimension038
  AngleOverride = false
  Arbitrary = false
  ArbitraryTolerances = false
  EqualTolerance = true
  ExtensionAngle = 0
  FormatSpec = %.2w
  FormatSpecOverTolerance = %+.2w
  FormatSpecUnderTolerance = %+.2w
  Inverted = false
  LineAngle = 0
  LockPosition = false
  MeasureType = 1
  OverTolerance = 0.05
  References2D = -> [View002]
  Rotation = 0
  Scale = 2
  ScaleType = 0
  TheoreticalExact = false
  Type = 2
  UnderTolerance = -0.05
  X = -63.5296
  Y = 1.33773
FEATURE [TechDraw::DrawViewDimension] Dimension039
  AngleOverride = false
  Arbitrary = false
  ArbitraryTolerances = false
  EqualTolerance = true
  ExtensionAngle = 0
  FormatSpec = R%.2w
  FormatSpecOverTolerance = %+.2w
  FormatSpecUnderTolerance = %+.2w
  Inverted = false
  LineAngle = 0
  LockPosition = false
  MeasureType = 1
  OverTolerance = 0
  References2D = -> [ComplexSection]
  Rotation = 0
  Scale = 2
  ScaleType = 0
  TheoreticalExact = false
  Type = 4
  UnderTolerance = 0
  X = -24.8071
  Y = 25.4275
FEATURE [TechDraw::DrawViewDimension] Dimension
  AngleOverride = false
  Arbitrary = false
  ArbitraryTolerances = false
  EqualTolerance = true
  ExtensionAngle = 0
  FormatSpec = R%.2w
  FormatSpecOverTolerance = %+.2w
  FormatSpecUnderTolerance = %+.2w
  Inverted = false
  LineAngle = 0
  LockPosition = false
  MeasureType = 1
  OverTolerance = 0
  References2D = -> [ComplexSection]
  Rotation = 0
  Scale = 2
  ScaleType = 0
  TheoreticalExact = false
  Type = 4
  UnderTolerance = 0
  X = -22.3763
  Y = 37.775
FEATURE [TechDraw::DrawViewDimension] Dimension040
  AngleOverride = false
  Arbitrary = false
  ArbitraryTolerances = false
  EqualTolerance = true
  ExtensionAngle = 0
  FormatSpec = %.2w
  FormatSpecOverTolerance = %+.2w
  FormatSpecUnderTolerance = %+.2w
  Inverted = false
  LineAngle = 0
  LockPosition = false
  MeasureType = 1
  OverTolerance = 0
  References2D = -> [ComplexSection]
  Rotation = 0
  Scale = 2
  ScaleType = 0
  TheoreticalExact = false
  Type = 2
  UnderTolerance = 0
  X = 50.8041
  Y = -1.3095
FEATURE [TechDraw::DrawViewDimension] Dimension041
  AngleOverride = false
  Arbitrary = false
  ArbitraryTolerances = false
  EqualTolerance = true
  ExtensionAngle = 0
  FormatSpec = %.2w
  FormatSpecOverTolerance = %+.2w
  FormatSpecUnderTolerance = %+.2w
  Inverted = false
  LineAngle = 0
  LockPosition = false
  MeasureType = 1
  OverTolerance = 0
  References2D = -> [View]
  Rotation = 0
  Scale = 2
  ScaleType = 0
  TheoreticalExact = false
  Type = 2
  UnderTolerance = 0
  X = 49.3362
  Y = 2.45968
FEATURE [TechDraw::DrawViewDimension] Dimension042
  AngleOverride = false
  Arbitrary = false
  ArbitraryTolerances = false
  EqualTolerance = true
  ExtensionAngle = 0
  FormatSpec = 12× %.2w
  FormatSpecOverTolerance = %+.2w
  FormatSpecUnderTolerance = %+.2w
  Inverted = false
  LineAngle = 0
  LockPosition = false
  MeasureType = 1
  OverTolerance = 0
  References2D = -> [View001]
  Rotation = 0
  Scale = 2
  ScaleType = 0
  TheoreticalExact = false
  Type = 2
  UnderTolerance = 0
  X = -47.1912
  Y = 0.484682
FEATURE [TechDraw::DrawViewDimension] Dimension043
  AngleOverride = false
  Arbitrary = false
  ArbitraryTolerances = false
  EqualTolerance = true
  ExtensionAngle = 0
  FormatSpec = %.2w
  FormatSpecOverTolerance = %+.2w
  FormatSpecUnderTolerance = %+.2w
  Inverted = false
  LineAngle = 0
  LockPosition = false
  MeasureType = 1
  OverTolerance = 0
  References2D = -> [View002]
  Rotation = 0
  Scale = 2
  ScaleType = 0
  TheoreticalExact = false
  Type = 2
  UnderTolerance = 0
  X = -53.6468
  Y = 6.7345
FEATURE [TechDraw::DrawViewBalloon] Balloon005
  BubbleShape = 2
  EndType = 0
  EndTypeScale = 1
  KinkLength = 5
  LockPosition = false
  OriginX = 14.2219
  OriginY = 15.3271
  Rotation = 0
  Scale = 2
  ScaleType = 0
  ShapeScale = 1
  SourceView = -> ComplexSection
  Text = 3
  TextWrapLen = -1
  X = 8.32091
  Y = 13.2809
FEATURE [TechDraw::DrawPage] Page  label="KNOB-TEK2_Drawing"
  KeepUpdated = true
  NextBalloonIndex = 10
  ProjectionType = 0
  Scale = 2
  Template = -> Template
  Views = -> [View,ComplexSection,View001,View002,Dimension010,Dimension014,Annotation,Dimension016,View003,View004,Annotation001,Balloon003,Dimension027,DimExtent,Balloon,Dimension029,Balloon004,Dimension030,Dimension033,Dimension038,Dimension039,Dimension,Dimension040,Dimension041,Dimension042,Dimension043,Balloon005]
---- part ../Design/PLASTIC-LOW-PROFILE-KEYCAP/PLASTIC-LOW-PROFILE-KEYCAP_THT.FCStd = doc fcstd_4af1fd4e1895 ----
FCSTD DOCUMENT  (FreeCAD 1.0R39319 (Git))
Label: PLASTIC-LOW-PROFILE-KEYCAP_THT
License: All rights reserved
LicenseURL: https://en.wikipedia.org/wiki/All_rights_reserved
objects: Sketcher::SketchObject×10, PartDesign::Pad×3, PartDesign::Pocket×2, PartDesign::Plane×1, PartDesign::SubtractivePipe×1, PartDesign::Mirrored×1, PartDesign::CoordinateSystem×1, PartDesign::Body×1
note: 43 computed .brp shape members not serialized (recipe doc carries the construction recipe); baked Part::Feature solids carry a one-line shape summary decoded from their .brp

FEATURE [Sketcher::SketchObject] Sketch
  ArcFitTolerance = 0
  AttachmentSupport = -> [XY_Plane]
  FullyConstrained = true
  MakeInternals = false
  MapMode = 5
  sketch-geometry (5):
    g0: LineSegment StartX=-9 StartY=-9 StartZ=0 EndX=-9 EndY=9 EndZ=0
    g1: LineSegment StartX=-9 StartY=9 StartZ=0 EndX=0 EndY=9 EndZ=0
    g2: LineSegment StartX=0 StartY=-9 StartZ=0 EndX=-9 EndY=-9 EndZ=0
    g3: GeomPoint [constr] X=0 Y=0 Z=0
    g4: LineSegment StartX=0 StartY=9 StartZ=0 EndX=0 EndY=-9 EndZ=0
  constraints (12):
    c: Horizontal(g2)
    c: Vertical(g0)
    c: Coincident(g3,g-1)
    c: Vertical(g4)
    c: Coincident(g1,g4)
    c: Coincident(g2,g4)
    c: Horizontal(g1)
    c: Symmetric(g2,g1,g3)
    c: DistanceY(g4,g4) = 18
    c: DistanceX(g0,g1) = 9
    c: Coincident(g0,g2)
    c: Coincident(g0,g1)
FEATURE [PartDesign::Pad] Pad
  Direction = (0,0,1)
  Length = 2.7
  Length2 = 10
  Profile = -> Sketch
  ReferenceAxis = -> Sketch [N_Axis]
  Refine = true
  Suppressed = false
  Type = 0
FEATURE [Sketcher::SketchObject] Sketch001
  ArcFitTolerance = 0
  AttachmentSupport = -> [XZ_Plane]
  FullyConstrained = false
  MakeInternals = false
  MapMode = 5
  Placement = pos=(0,0,0) rot=(1,0,0;1.5708rad)
  sketch-geometry (12):
    g0: LineSegment StartX=-9 StartY=2.7 StartZ=0 EndX=0 EndY=2.7 EndZ=0
    g1: LineSegment StartX=0 StartY=3 StartZ=0 EndX=0 EndY=2.7 EndZ=0
    g2: LineSegment StartX=-9 StartY=2.7 StartZ=0 EndX=-9 EndY=3.5 EndZ=0
    g3-g7: Circle [constr] x5 (B-spline internal-alignment scaffolding for g8; pole/knot coordinates omitted)
    g8: BSplineCurve PolesCount=5 KnotsCount=3 Degree=3 IsPeriodic=0
    g9: GeomPoint [constr] X=0 Y=3 Z=0
    g10: GeomPoint [constr] X=-5.37681 Y=3.56724 Z=0
    g11: GeomPoint [constr] X=-9 Y=3.5 Z=0
  constraints (18):
    c: Horizontal(g0)
    c: PointOnObject(g0,g-2)
    c: DistanceY(g-1,g0) = 2.7
    c: DistanceX(g0,g0) = 9
    c: PointOnObject(g1,g-2)
    c: Coincident(g1,g0)
    c: Coincident(g2,g0)
    c: Vertical(g2)
    c: DistanceY(g1,g1) = 0.3
    c: Weight(g3) = 1
    c: Coincident(g8,g1)
    c: Equal(g3, g4-g7) x4
    c: Coincident(g8,g2)
    c: InternalAlignment(g3-g7 -> g8) x5
    c: InternalAlignment(g9,g8)
    c: InternalAlignment(g10,g8)
    c: InternalAlignment(g11,g8)
    c: Distance(g2,g-1) = 3.5
FEATURE [PartDesign::Pad] Pad001
  BaseFeature = -> Pad
  Direction = (0,-1,2e-16)
  Length = 18
  Length2 = 10
  Midplane = true
  Profile = -> Sketch001
  ReferenceAxis = -> Sketch001 [N_Axis]
  Refine = true
  Suppressed = false
  Type = 0
FEATURE [Sketcher::SketchObject] Sketch002
  ArcFitTolerance = 0
  AttachmentSupport = -> [XY_Plane]
  FullyConstrained = true
  MakeInternals = false
  MapMode = 5
  sketch-geometry (14):
    g0: LineSegment [constr] StartX=0 StartY=9 StartZ=0 EndX=-7 EndY=9 EndZ=0
    g1: LineSegment [constr] StartX=-9 StartY=7 StartZ=0 EndX=-9 EndY=-7 EndZ=0
    g2: LineSegment [constr] StartX=-7 StartY=-9 StartZ=0 EndX=0 EndY=-9 EndZ=0
    g3: LineSegment [constr] StartX=0 StartY=-9 StartZ=0 EndX=0 EndY=9 EndZ=0
    g4: ArcOfCircle CenterX=-7 CenterY=7 CenterZ=0 NormalX=0 NormalY=0 NormalZ=1 AngleXU=0 Radius=2 StartAngle=1.5708 EndAngle=3.14159
    g5: ArcOfCircle CenterX=-7 CenterY=-7 CenterZ=0 NormalX=0 NormalY=0 NormalZ=1 AngleXU=0 Radius=2 StartAngle=3.14159 EndAngle=4.71239
    g6: LineSegment StartX=-9 StartY=7 StartZ=0 EndX=-10 EndY=7 EndZ=0
    g7: LineSegment StartX=-10 StartY=7 StartZ=0 EndX=-10 EndY=10 EndZ=0
    g8: LineSegment StartX=-10 StartY=10 StartZ=0 EndX=-7 EndY=10 EndZ=0
    g9: LineSegment StartX=-9 StartY=-7 StartZ=0 EndX=-10 EndY=-7 EndZ=0
    g10: LineSegment StartX=-7 StartY=-9 StartZ=0 EndX=-7 EndY=-10 EndZ=0
    g11: LineSegment StartX=-10 StartY=-7 StartZ=0 EndX=-10 EndY=-10 EndZ=0
    g12: LineSegment StartX=-10 StartY=-10 StartZ=0 EndX=-7 EndY=-10 EndZ=0
    g13: LineSegment StartX=-7 StartY=10 StartZ=0 EndX=-7 EndY=9 EndZ=0
  constraints (37):
    c: Coincident(g2,g3)
    c: Coincident(g3,g0)
    c: Horizontal(g0)
    c: Horizontal(g2)
    c: Vertical(g1)
    c: Vertical(g3)
    c: Symmetric(g0,g2,g-1)
    c: Tangent(g0,g4) = -1.5708
    c: Tangent(g1,g4) = -1.5708
    c: Tangent(g1,g5) = -1.5708
    c: Tangent(g2,g5) = -1.5708
    c: Equal(g4,g5)
    c: Diameter(g4) = 4
    c: DistanceY(g3,g3) = 18
    c: DistanceX(g1,g0) = 9
    c: Coincident(g6,g4)
    c: Coincident(g7,g6)
    c: Vertical(g7)
    c: Coincident(g8,g7)
    c: Coincident(g9,g5)
    c: Horizontal(g9)
    c: Coincident(g10,g5)
    c: Coincident(g11,g9)
    c: Vertical(g11)
    c: Coincident(g12,g10)
    c: Horizontal(g12)
    c: Coincident(g11,g12)
    c: Vertical(g10)
    c: Horizontal(g8)
    c: Horizontal(g6)
    c: Equal(g6,g10)
    c: Equal(g10,g9)
    c: Coincident(g13,g8)
    c: Coincident(g13,g4)
    c: Vertical(g13)
    c: DistanceX(g6,g4) = 1
    c: Equal(g6,g13)
FEATURE [PartDesign::Pocket] Pocket
  BaseFeature = -> Pad001
  Direction = (0,0,-1)
  Length = 10
  Length2 = 5
  Profile = -> Sketch002
  ReferenceAxis = -> Sketch002 [N_Axis]
  Refine = true
  Reversed = true
  Suppressed = false
  Type = 0
FEATURE [Sketcher::SketchObject] Sketch003
  ArcFitTolerance = 0
  AttachmentSupport = -> [XY_Plane]
  FullyConstrained = true
  MakeInternals = false
  MapMode = 5
  sketch-geometry (7):
    g0: LineSegment StartX=-7.0342e-12 StartY=7.8 StartZ=0 EndX=-6.25 EndY=7.8 EndZ=0
    g1: LineSegment StartX=-7.75 StartY=6.3 StartZ=0 EndX=-7.75 EndY=-6.3 EndZ=0
    g2: LineSegment StartX=-6.25 StartY=-7.8 StartZ=0 EndX=0 EndY=-7.8 EndZ=0
    g3: LineSegment StartX=0 StartY=-7.8 StartZ=0 EndX=0 EndY=0 EndZ=0
    g4: ArcOfCircle CenterX=-6.25 CenterY=6.3 CenterZ=0 NormalX=0 NormalY=0 NormalZ=1 AngleXU=0 Radius=1.5 StartAngle=1.5708 EndAngle=3.14159
    g5: ArcOfCircle CenterX=-6.25 CenterY=-6.3 CenterZ=0 NormalX=0 NormalY=0 NormalZ=1 AngleXU=0 Radius=1.5 StartAngle=3.14159 EndAngle=4.71239
    g6: LineSegment StartX=0 StartY=0 StartZ=0 EndX=-7.0342e-12 EndY=7.8 EndZ=0
  constraints (17):
    c: Coincident(g2,g3)
    c: Coincident(g6,g0)
    c: Horizontal(g0)
    c: Horizontal(g2)
    c: Vertical(g1)
    c: Vertical(g3)
    c: Symmetric(g0,g2,g-1)
    c: Tangent(g0,g4) = -1.5708
    c: Tangent(g1,g4) = -1.5708
    c: Tangent(g1,g5) = -1.5708
    c: Tangent(g2,g5) = -1.5708
    c: Equal(g4,g5)
    c: Diameter(g4) = 3
    c: DistanceX(g1,g0) = 7.75
    c: DistanceY(g3,g6) = 15.6
    c: Coincident(g3,g6)
    c: Coincident(g3,g-1)
FEATURE [PartDesign::Pocket] Pocket001
  BaseFeature = -> Pocket
  Direction = (0,0,-1)
  Length = 1.7
  Length2 = 5
  Profile = -> Sketch003
  ReferenceAxis = -> Sketch003 [N_Axis]
  Reversed = true
  Suppressed = false
  Type = 0
FEATURE [Sketcher::SketchObject] Sketch004
  ArcFitTolerance = 0
  AttachmentSupport = -> [Pocket001]
  FullyConstrained = true
  MakeInternals = false
  MapMode = 5
  Placement = pos=(0,0,1.7) rot=(1,0,0;3.14159rad)
  sketch-geometry (11):
    g0: ArcOfCircle CenterX=0 CenterY=0 CenterZ=0 NormalX=0 NormalY=0 NormalZ=1 AngleXU=0 Radius=2.75 StartAngle=1.5708 EndAngle=4.71239
    g1: ArcOfCircle CenterX=0 CenterY=0 CenterZ=0 NormalX=0 NormalY=0 NormalZ=1 AngleXU=0 Radius=2.09688 StartAngle=1.5708 EndAngle=1.87596
    g2: LineSegment StartX=1e-16 StartY=2.75 StartZ=0 EndX=1e-16 EndY=2.09688 EndZ=0
    g3: LineSegment StartX=-5e-16 StartY=-2.09688 StartZ=0 EndX=-5e-16 EndY=-2.75 EndZ=0
    g4: LineSegment StartX=-2 StartY=0.63 StartZ=0 EndX=-0.63 EndY=0.63 EndZ=0
    g5: LineSegment StartX=-0.63 StartY=0.63 StartZ=0 EndX=-0.63 EndY=2 EndZ=0
    g6: LineSegment StartX=-2 StartY=-0.63 StartZ=0 EndX=-0.63 EndY=-0.63 EndZ=0
    g7: LineSegment StartX=-0.63 StartY=-0.63 StartZ=0 EndX=-0.63 EndY=-2 EndZ=0
    g8: ArcOfCircle CenterX=0 CenterY=0 CenterZ=0 NormalX=0 NormalY=0 NormalZ=1 AngleXU=0 Radius=2.09688 StartAngle=2.83643 EndAngle=3.44675
    g9: ArcOfCircle CenterX=0 CenterY=0 CenterZ=0 NormalX=0 NormalY=0 NormalZ=1 AngleXU=0 Radius=2.09688 StartAngle=4.40723 EndAngle=4.71239
    g10: LineSegment [constr] StartX=-2.09688 StartY=0 StartZ=0 EndX=-2.75 EndY=0 EndZ=0
  constraints (35):
    c: Coincident(g0,g-1)
    c: Coincident(g1,g0)
    c: Vertical(g2)
    c: PointOnObject(g2,g-2)
    c: Coincident(g0,g3)
    c: Coincident(g0,g2)
    c: Coincident(g2,g1)
    c: Coincident(g3,g9)
    c: Horizontal(g4)
    c: Coincident(g5,g4)
    c: Vertical(g5)
    c: PointOnObject(g6,g1)
    c: Horizontal(g6)
    c: Coincident(g7,g6)
    c: PointOnObject(g7,g1)
    c: Vertical(g7)
    c: Symmetric(g4,g6,g-1)
    c: Equal(g1,g8)
    c: Coincident(g1,g5)
    c: Coincident(g8,g4)
    c: Coincident(g1,g8)
    c: Equal(g8,g9)
    c: PointOnObject(g8,g6)
    c: PointOnObject(g9,g7)
    c: Coincident(g8,g9)
    c: DistanceY(g6,g4) = 1.26
    c: DistanceX(g1,g0) = 0.63
    c: DistanceX(g4,g0) = 2
    c: PointOnObject(g10,g8)
    c: PointOnObject(g10,g0)
    c: PointOnObject(g10,g-1)
    c: PointOnObject(g10,g-1)
    c: Vertical(g3)
    c: PointOnObject(g3,g-2)
    c: Diameter(g0) = 5.5
FEATURE [PartDesign::Pad] Pad002
  BaseFeature = -> Pocket001
  Direction = (0,0,-1)
  Length = 3.4
  Length2 = 10
  Profile = -> Sketch004
  ReferenceAxis = -> Sketch004 [N_Axis]
  Suppressed = false
  Type = 0
FEATURE [Sketcher::SketchObject] Sketch005
  ArcFitTolerance = 0
  AttachmentSupport = -> [XY_Plane]
  FullyConstrained = true
  MakeInternals = false
  MapMode = 5
  sketch-geometry (13):
    g0: LineSegment StartX=-2.22 StartY=-1.5 StartZ=0 EndX=-3.48 EndY=-1.5 EndZ=0
    g1: LineSegment StartX=-3.48 StartY=-1.5 StartZ=0 EndX=-3.48 EndY=-0.5 EndZ=0
    g2: LineSegment StartX=-3.48 StartY=-0.5 StartZ=0 EndX=-3.35 EndY=-0.5 EndZ=0
    g3: LineSegment StartX=-2.22 StartY=-0.5 StartZ=0 EndX=-2.22 EndY=-1.5 EndZ=0
    g4: LineSegment StartX=-2.22 StartY=0.5 StartZ=0 EndX=-2.35 EndY=0.5 EndZ=0
    g5: LineSegment StartX=-3.48 StartY=0.5 StartZ=0 EndX=-3.48 EndY=1.5 EndZ=0
    g6: LineSegment StartX=-3.48 StartY=1.5 StartZ=0 EndX=-2.22 EndY=1.5 EndZ=0
    g7: LineSegment StartX=-2.22 StartY=1.5 StartZ=0 EndX=-2.22 EndY=0.5 EndZ=0
    g8: LineSegment StartX=-2.35 StartY=-0.5 StartZ=0 EndX=-2.35 EndY=0.5 EndZ=0
    g9: LineSegment StartX=-3.35 StartY=-0.5 StartZ=0 EndX=-3.35 EndY=0.5 EndZ=0
    g10: LineSegment StartX=-2.35 StartY=-0.5 StartZ=0 EndX=-2.22 EndY=-0.5 EndZ=0
    g11: LineSegment StartX=-3.35 StartY=0.5 StartZ=0 EndX=-3.48 EndY=0.5 EndZ=0
    g12: GeomPoint [constr] X=-2.85 Y=-1.5 Z=0
  constraints (36):
    c: Coincident(g0,g1)
    c: Coincident(g1,g2)
    c: Coincident(g10,g3)
    c: Coincident(g3,g0)
    c: Horizontal(g0)
    c: Horizontal(g2)
    c: Vertical(g1)
    c: Vertical(g3)
    c: Coincident(g11,g5)
    c: Coincident(g5,g6)
    c: Coincident(g6,g7)
    c: Coincident(g7,g4)
    c: Horizontal(g4)
    c: Horizontal(g6)
    c: Vertical(g5)
    c: Vertical(g7)
    c: Vertical(g8)
    c: Vertical(g1,g11)
    c: Vertical(g10,g4)
    c: Coincident(g2,g9)
    c: Coincident(g10,g8)
    c: Coincident(g4,g8)
    c: Coincident(g11,g9)
    c: Equal(g2,g10)
    c: Equal(g1,g5)
    c: Symmetric(g2,g9,g-1)
    c: Horizontal(g11)
    c: Horizontal(g2,g8)
    c: Horizontal(g4,g9)
    c: Horizontal(g10)
    c: Symmetric(g0,g0,g12)
    c: DistanceX(g12,g-1) = 2.85
    c: DistanceX(g0,g0) = 1.26
    c: DistanceX(g2,g8) = 1
    c: DistanceY(g0,g5) = 3
    c: DistanceY(g1,g1) = 1
FEATURE [Sketcher::SketchObject] Sketch006
  ArcFitTolerance = 0
  AttachmentSupport = -> [XZ_Plane]
  FullyConstrained = false
  MakeInternals = false
  MapMode = 5
  Placement = pos=(0,0,0) rot=(1,0,0;1.5708rad)
  sketch-geometry (30):
    g0: LineSegment StartX=-15 StartY=-2.3 StartZ=0 EndX=-15 EndY=-1.3 EndZ=0
    g1: LineSegment StartX=-15 StartY=-1.3 StartZ=0 EndX=15 EndY=-1.3 EndZ=0
    g2: LineSegment StartX=15 StartY=-1.3 StartZ=0 EndX=15 EndY=-2.3 EndZ=0
    g3: LineSegment StartX=15 StartY=-2.3 StartZ=0 EndX=-15 EndY=-2.3 EndZ=0
    g4: GeomPoint [constr] X=0 Y=-1.8 Z=0
    g5: LineSegment StartX=-15 StartY=-12.4 StartZ=0 EndX=-15 EndY=-10.8 EndZ=0
    g6: LineSegment StartX=-15 StartY=-10.8 StartZ=0 EndX=15 EndY=-10.8 EndZ=0
    g7: LineSegment StartX=15 StartY=-10.8 StartZ=0 EndX=15 EndY=-12.4 EndZ=0
    g8: LineSegment StartX=15 StartY=-12.4 StartZ=0 EndX=-15 EndY=-12.4 EndZ=0
    g9: GeomPoint [constr] X=0 Y=-11.6 Z=0
    g10: LineSegment [constr] StartX=-7.5 StartY=-8 StartZ=0 EndX=-7.5 EndY=-3 EndZ=0
    g11: LineSegment [constr] StartX=-7.5 StartY=-3 StartZ=0 EndX=7.5 EndY=-3 EndZ=0
    g12: LineSegment [constr] StartX=7.5 StartY=-3 StartZ=0 EndX=7.5 EndY=-8 EndZ=0
    g13: LineSegment [constr] StartX=7.5 StartY=-8 StartZ=0 EndX=-7.5 EndY=-8 EndZ=0
    g14: GeomPoint [constr] X=0 Y=-5.5 Z=0
    g15: LineSegment StartX=-11.0572 StartY=-9 StartZ=0 EndX=-11.0572 EndY=-8 EndZ=0
    g16: LineSegment StartX=-11.0572 StartY=-8 StartZ=0 EndX=11.0572 EndY=-8 EndZ=0
    g17: LineSegment StartX=11.0572 StartY=-8 StartZ=0 EndX=11.0572 EndY=-9 EndZ=0
    g18: GeomPoint [constr] X=0 Y=-8.5 Z=0
    g19: LineSegment StartX=-11.0572 StartY=-9 StartZ=0 EndX=11.0572 EndY=-9 EndZ=0
    g20: LineSegment StartX=-3.7807 StartY=-10.8 StartZ=0 EndX=-3.7807 EndY=-9 EndZ=0
    g21: LineSegment StartX=-3.7807 StartY=-9 StartZ=0 EndX=3.7807 EndY=-9 EndZ=0
    g22: LineSegment StartX=3.7807 StartY=-9 StartZ=0 EndX=3.7807 EndY=-10.8 EndZ=0
    g23: LineSegment StartX=3.7807 StartY=-10.8 StartZ=0 EndX=-3.7807 EndY=-10.8 EndZ=0
    g24: GeomPoint [constr] X=0 Y=-9.9 Z=0
    g25: LineSegment StartX=-5.52707 StartY=-3 StartZ=0 EndX=-5.52707 EndY=0 EndZ=0
    g26: LineSegment StartX=-5.52707 StartY=0 StartZ=0 EndX=5.52707 EndY=0 EndZ=0
    g27: LineSegment StartX=5.52707 StartY=0 StartZ=0 EndX=5.52707 EndY=-3 EndZ=0
    g28: LineSegment StartX=5.52707 StartY=-3 StartZ=0 EndX=-5.52707 EndY=-3 EndZ=0
    g29: GeomPoint [constr] X=0 Y=-1.5 Z=0
  constraints (75):
    c: Coincident(g0,g1)
    c: Coincident(g1,g2)
    c: Coincident(g2,g3)
    c: Coincident(g3,g0)
    c: Horizontal(g1)
    c: Horizontal(g3)
    c: Vertical(g0)
    c: Vertical(g2)
    c: Symmetric(g1,g0,g4)
    c: PointOnObject(g4,g-2)
    c: Coincident(g5,g6)
    c: Coincident(g6,g7)
    c: Coincident(g7,g8)
    c: Coincident(g8,g5)
    c: Horizontal(g6)
    c: Horizontal(g8)
    c: Vertical(g5)
    c: Vertical(g7)
    c: Symmetric(g6,g5,g9)
    c: PointOnObject(g9,g-2)
    c: DistanceY(g7,g7) = 1.6
    c: DistanceY(g2,g2) = 1
    c: Equal(g3,g6)
    c: DistanceX(g8,g8) = 30
    c: DistanceY(g6,g2) = 8.5
    c: DistanceY(g5,g-1) = 10.8
    c: Coincident(g10,g11)
    c: Coincident(g11,g12)
    c: Coincident(g12,g13)
    c: Coincident(g13,g10)
    c: Horizontal(g11)
    c: Horizontal(g13)
    c: Vertical(g10)
    c: Vertical(g12)
    c: Symmetric(g11,g10,g14)
    c: PointOnObject(g14,g-2)
    c: DistanceY(g12,g12) = 5
    c: DistanceX(g13,g13) = 15
    c: Coincident(g15,g16)
    c: Coincident(g16,g17)
    c: Horizontal(g16)
    c: Vertical(g15)
    c: Vertical(g17)
    c: Symmetric(g16,g15,g18)
    c: PointOnObject(g18,g-2)
    c: PointOnObject(g12,g16)
    c: DistanceY(g17,g17) = 1
    c: Coincident(g19,g15)
    c: Coincident(g19,g17)
    c: Horizontal(g19)
    c: Coincident(g20,g21)
    c: Coincident(g21,g22)
    c: Coincident(g22,g23)
    c: Coincident(g23,g20)
    c: Horizontal(g21)
    c: Horizontal(g23)
    c: Vertical(g20)
    c: Vertical(g22)
    c: Symmetric(g21,g20,g24)
    c: PointOnObject(g24,g-2)
    c: DistanceY(g22,g22) = 1.8
    c: PointOnObject(g21,g19)
    c: PointOnObject(g22,g6)
    c: Coincident(g25,g26)
    c: Coincident(g26,g27)
    c: Coincident(g27,g28)
    c: Coincident(g28,g25)
    c: Horizontal(g26)
    c: Horizontal(g28)
    c: Vertical(g25)
    c: Vertical(g27)
    c: Symmetric(g26,g25,g29)
    c: PointOnObject(g29,g-2)
    c: PointOnObject(g26,g-1)
    c: PointOnObject(g27,g11)
FEATURE [Sketcher::SketchObject] Sketch007
  ArcFitTolerance = 0
  AttachmentSupport = -> [XZ_Plane]
  FullyConstrained = false
  MakeInternals = false
  MapMode = 5
  Placement = pos=(0,0,0) rot=(1,0,0;1.5708rad)
  sketch-geometry (14):
    g0: LineSegment StartX=-8.25 StartY=2.85 StartZ=0 EndX=0 EndY=2.85 EndZ=0
    g1-g6: Circle [constr] x6 (B-spline internal-alignment scaffolding for g7; pole/knot coordinates omitted)
    g7: BSplineCurve PolesCount=6 KnotsCount=4 Degree=3 IsPeriodic=0
    g8-g11: GeomPoint [constr] x4 (B-spline internal-alignment scaffolding for g7; pole/knot coordinates omitted)
    g12: GeomPoint [constr] X=-7.09131 Y=3.79 Z=0
    g13: LineSegment StartX=0 StartY=2.94891 StartZ=0 EndX=0 EndY=2.85 EndZ=0
  constraints (14):
    c: Horizontal(g0)
    c: PointOnObject(g0,g-2)
    c: DistanceY(g-1,g0) = 2.85
    c: DistanceX(g0,g0) = 8.25
    c: Weight(g1) = 1
    c: Coincident(g7,g0)
    c: Equal(g1, g2-g6) x5
    c: PointOnObject(g7,g-2)
    c: InternalAlignment(g1-g6 -> g7) x6
    c: InternalAlignment(g8-g11 -> g7) x4
    c: PointOnObject(g12,g7)
    c: DistanceY(g0,g12) = 0.94
    c: Coincident(g13,g7)
    c: Coincident(g13,g0)
FEATURE [Sketcher::SketchObject] Sketch008
  ArcFitTolerance = 1e-06
  AttachmentSupport = -> [YZ_Plane]
  FullyConstrained = true
  MakeInternals = false
  MapMode = 5
  Placement = pos=(0,0,0) rot=(0.57735,0.57735,0.57735;2.0944rad)
  sketch-geometry (3):
    g0: LineSegment StartX=-9 StartY=2.4 StartZ=0 EndX=-7.5 EndY=4.05 EndZ=0
    g1: LineSegment StartX=-7.5 StartY=4.05 StartZ=0 EndX=-9 EndY=4.05 EndZ=0
    g2: LineSegment StartX=-9 StartY=4.05 StartZ=0 EndX=-9 EndY=2.4 EndZ=0
  constraints (9):
    c: Coincident(g1,g0)
    c: Coincident(g2,g1)
    c: Coincident(g2,g0)
    c: Vertical(g2)
    c: Distance(g0,g-1) = 2.4
    c: Horizontal(g1)
    c: Distance(g-1,g1) = 4.05
    c: Distance(g-2,g2) = 9
    c: DistanceX(g1,g1) = 1.5
FEATURE [PartDesign::Plane] DatumPlane
  AttachmentOffset = pos=(0,0,2.4) rot=(0,0,1;0rad)
  AttachmentSupport = -> [Sketch008]
  Length = 60
  MapMode = 3
  Placement = pos=(0,0,2.4) rot=(0,0,-1;1.5708rad)
  ResizeMode = 0
  Width = 60
FEATURE [Sketcher::SketchObject] Sketch009
  ArcFitTolerance = 1e-06
  AttachmentSupport = -> [DatumPlane]
  FullyConstrained = true
  MakeInternals = false
  MapMode = 5
  Placement = pos=(0,0,2.4) rot=(0,0,-1;1.5708rad)
  sketch-geometry (7):
    g0: LineSegment StartX=-9 StartY=-8e-16 StartZ=0 EndX=-9 EndY=-7 EndZ=0
    g1: LineSegment StartX=-7 StartY=-9 StartZ=0 EndX=7 EndY=-9 EndZ=0
    g2: LineSegment StartX=9 StartY=-7 StartZ=0 EndX=9 EndY=9e-16 EndZ=0
    g3: ArcOfCircle CenterX=-7 CenterY=-7 CenterZ=0 NormalX=0 NormalY=0 NormalZ=1 AngleXU=0 Radius=2 StartAngle=3.14159 EndAngle=4.71239
    g4: GeomPoint [constr] X=-9 Y=-9 Z=0
    g5: ArcOfCircle CenterX=7 CenterY=-7 CenterZ=0 NormalX=0 NormalY=0 NormalZ=1 AngleXU=0 Radius=2 StartAngle=4.71239 EndAngle=6.28319
    g6: GeomPoint [constr] X=9 Y=-9 Z=0
  constraints (17):
    c: Vertical(g0)
    c: Horizontal(g1)
    c: Vertical(g2)
    c: PointOnObject(g4,g0)
    c: PointOnObject(g4,g1)
    c: Tangent(g0,g3) = -1.5708
    c: Tangent(g1,g3) = -1.5708
    c: PointOnObject(g6,g2)
    c: PointOnObject(g6,g1)
    c: Tangent(g2,g5) = -1.5708
    c: Tangent(g1,g5) = -1.5708
    c: Equal(g0,g2)
    c: Distance(g1,g-1) = 9
    c: Distance(g2,g0) = 18
    c: Radius(g5) = 2
    c: Symmetric(g0,g2,g-1)
    c: Equal(g5,g3)
FEATURE [PartDesign::SubtractivePipe] SubtractivePipe
  AuxilleryCurvelinear = true
  AuxillerySpineTangent = false
  BaseFeature = -> Pad002
  Binormal = (0,0,0)
  Mode = 0
  Profile = -> Sketch008
  Refine = true
  Spine = -> Sketch009
  SpineTangent = false
  Suppressed = false
  Transformation = 0
  Transition = 1
FEATURE [PartDesign::Mirrored] Mirrored
  BaseFeature = -> SubtractivePipe
  MirrorPlane = -> YZ_Plane
  Refine = true
  Suppressed = false
  TransformMode = 1
FEATURE [PartDesign::CoordinateSystem] LCS_1
  AttacherType = Attacher::AttachEngine3D
  AttachmentSupport = -> [Mirrored]
  MapMode = 11
  Placement = pos=(0,0,1.7) rot=(0,1,0;3.14159rad)
FEATURE [PartDesign::Body] Body  label="PLASTIC-LOW-PROFILE-KEYCAP"
  AllowCompound = false
  Group = -> [Sketch,Pad,Sketch001,Pad001,Sketch002,Pocket,Sketch003,Pocket001,Sketch004,Pad002,Sketch005,Sketch006,Sketch007,Sketch008,DatumPlane,Sketch009,SubtractivePipe,Mirrored,LCS_1]
  Origin = -> Origin
  Tip = -> Mirrored
---- part ../Design/PLASTIC-TEK2-KNOB-INTERFACE/PLASTIC-TEK2-KNOB-INTERFACE.FCStd = doc fcstd_a0d65299c5b8 ----
FCSTD DOCUMENT  (FreeCAD 1.0R39319 (Git))
Label: PLASTIC-TEK2-KNOB-INTERFACE
License: All rights reserved
LicenseURL: https://en.wikipedia.org/wiki/All_rights_reserved
objects: Sketcher::SketchObject×10, PartDesign::Pad×9, PartDesign::Plane×5, PartDesign::Chamfer×3, PartDesign::Body×3, PartDesign::CoordinateSystem×3, PartDesign::Boolean×2, PartDesign::Pocket×1
note: 74 computed .brp shape members not serialized (recipe doc carries the construction recipe); baked Part::Feature solids carry a one-line shape summary decoded from their .brp

FEATURE [Sketcher::SketchObject] Sketch
  ArcFitTolerance = 0
  AttachmentSupport = -> [XY_Plane]
  FullyConstrained = true
  MakeInternals = false
  MapMode = 5
  sketch-geometry (5):
    g0: LineSegment StartX=-2.81957 StartY=1.9 StartZ=0 EndX=2.81957 EndY=1.9 EndZ=0
    g1: ArcOfCircle CenterX=0 CenterY=0 CenterZ=0 NormalX=0 NormalY=0 NormalZ=1 AngleXU=0 Radius=3.4 StartAngle=2.54863 EndAngle=6.87615
    g2: LineSegment StartX=-4.71169 StartY=4.55 StartZ=0 EndX=4.71169 EndY=4.55 EndZ=0
    g3: GeomPoint [constr] X=1e-16 Y=4.55 Z=0
    g4: ArcOfCircle CenterX=0 CenterY=0 CenterZ=0 NormalX=0 NormalY=0 NormalZ=1 AngleXU=0 Radius=6.55 StartAngle=2.37365 EndAngle=7.05113
  constraints (13):
    c: Diameter(g1) = 6.8
    c: Coincident(g0,g1)
    c: Coincident(g0,g1)
    c: Horizontal(g0)
    c: Horizontal(g2)
    c: Symmetric(g2,g2,g3)
    c: Diameter(g4) = 13.1
    c: Coincident(g4,g2)
    c: Coincident(g4,g2)
    c: Coincident(g4,g1)
    c: DistanceY(g1,g2) = 4.55
    c: Coincident(g1,g-1)
    c: DistanceY(g1,g0) = 1.9
FEATURE [PartDesign::Pad] Pad
  Direction = (0,0,1)
  Length = 9.5
  Length2 = 10
  Midplane = true
  Profile = -> Sketch
  ReferenceAxis = -> Sketch [N_Axis]
  Suppressed = false
  Type = 0
FEATURE [Sketcher::SketchObject] Sketch002
  ArcFitTolerance = 0
  AttachmentSupport = -> [XY_Plane]
  FullyConstrained = true
  MakeInternals = false
  MapMode = 5
  sketch-geometry (41):
    g0: ArcOfCircle [constr] CenterX=0 CenterY=0 CenterZ=0 NormalX=0 NormalY=0 NormalZ=1 AngleXU=0 Radius=6.6 StartAngle=2.37043 EndAngle=7.05435
    g1: Circle CenterX=-5.65685 CenterY=3.4 CenterZ=0 NormalX=0 NormalY=0 NormalZ=1 AngleXU=0 Radius=0.5
    g2: LineSegment [constr] StartX=-4.73286 StartY=4.6 StartZ=0 EndX=4.73286 EndY=4.6 EndZ=0
    g3: Circle CenterX=-6.48224 CenterY=1.2412 CenterZ=0 NormalX=0 NormalY=0 NormalZ=1 AngleXU=0 Radius=0.5
    g4: Circle CenterX=-6.51272 CenterY=-1.0698 CenterZ=0 NormalX=0 NormalY=0 NormalZ=1 AngleXU=0 Radius=0.5
    g5: Circle CenterX=-4.27196 CenterY=-5.03094 CenterZ=0 NormalX=0 NormalY=0 NormalZ=1 AngleXU=0 Radius=0.5
    g6: Circle CenterX=-2.2755 CenterY=-6.19533 CenterZ=0 NormalX=0 NormalY=0 NormalZ=1 AngleXU=0 Radius=0.5
    g7: Circle CenterX=-4e-16 CenterY=-6.6 CenterZ=0 NormalX=0 NormalY=0 NormalZ=1 AngleXU=0 Radius=0.5
    g8: Circle CenterX=5.65685 CenterY=3.4 CenterZ=0 NormalX=0 NormalY=0 NormalZ=1 AngleXU=0 Radius=0.5
    g9: Circle CenterX=-5.74456 CenterY=-3.24962 CenterZ=0 NormalX=0 NormalY=0 NormalZ=1 AngleXU=0 Radius=0.5
    g10: Circle CenterX=6.48224 CenterY=1.2412 CenterZ=0 NormalX=0 NormalY=0 NormalZ=1 AngleXU=0 Radius=0.5
    g11: Circle CenterX=4.27196 CenterY=-5.03094 CenterZ=0 NormalX=0 NormalY=0 NormalZ=1 AngleXU=0 Radius=0.5
    g12: Circle CenterX=5.74456 CenterY=-3.24962 CenterZ=0 NormalX=0 NormalY=0 NormalZ=1 AngleXU=0 Radius=0.5
    g13: Circle CenterX=2.2755 CenterY=-6.19533 CenterZ=0 NormalX=0 NormalY=0 NormalZ=1 AngleXU=0 Radius=0.5
    g14: Circle CenterX=6.51272 CenterY=-1.0698 CenterZ=0 NormalX=0 NormalY=0 NormalZ=1 AngleXU=0 Radius=0.5
    g15: LineSegment [constr] StartX=-5.65685 StartY=3.4 StartZ=0 EndX=-6.48224 EndY=1.2412 EndZ=0
    g16: LineSegment [constr] StartX=-6.48224 StartY=1.2412 StartZ=0 EndX=-6.51272 EndY=-1.0698 EndZ=0
    g17: LineSegment [constr] StartX=-6.51272 StartY=-1.0698 StartZ=0 EndX=-5.74456 EndY=-3.24962 EndZ=0
    g18: LineSegment [constr] StartX=-5.74456 StartY=-3.24962 StartZ=0 EndX=-4.27196 EndY=-5.03094 EndZ=0
    g19: LineSegment [constr] StartX=-4.27196 StartY=-5.03094 StartZ=0 EndX=-2.2755 EndY=-6.19533 EndZ=0
    g20: LineSegment [constr] StartX=-2.2755 StartY=-6.19533 StartZ=0 EndX=-4e-16 EndY=-6.6 EndZ=0
    g21: LineSegment [constr] StartX=-4e-16 StartY=-6.6 StartZ=0 EndX=2.2755 EndY=-6.19533 EndZ=0
    g22: LineSegment [constr] StartX=2.2755 StartY=-6.19533 StartZ=0 EndX=4.27196 EndY=-5.03094 EndZ=0
    g23: LineSegment [constr] StartX=4.27196 StartY=-5.03094 StartZ=0 EndX=5.74456 EndY=-3.24962 EndZ=0
    g24: LineSegment [constr] StartX=5.74456 StartY=-3.24962 StartZ=0 EndX=6.51272 EndY=-1.0698 EndZ=0
    g25: LineSegment [constr] StartX=6.51272 StartY=-1.0698 StartZ=0 EndX=6.48224 EndY=1.2412 EndZ=0
    g26: LineSegment [constr] StartX=6.48224 StartY=1.2412 StartZ=0 EndX=5.65685 EndY=3.4 EndZ=0
    g27: Circle CenterX=-3.45 CenterY=4.6 CenterZ=0 NormalX=0 NormalY=0 NormalZ=1 AngleXU=0 Radius=0.5
    g28: Circle CenterX=-1.15 CenterY=4.6 CenterZ=0 NormalX=0 NormalY=0 NormalZ=1 AngleXU=0 Radius=0.5
    g29: LineSegment [constr] StartX=-3.45 StartY=4.6 StartZ=0 EndX=-1.15 EndY=4.6 EndZ=0
    g30: Circle CenterX=1.15 CenterY=4.6 CenterZ=0 NormalX=0 NormalY=0 NormalZ=1 AngleXU=0 Radius=0.5
    g31: LineSegment [constr] StartX=-1.15 StartY=4.6 StartZ=0 EndX=1.15 EndY=4.6 EndZ=0
    g32: Circle CenterX=3.45 CenterY=4.6 CenterZ=0 NormalX=0 NormalY=0 NormalZ=1 AngleXU=0 Radius=0.5
    g33: LineSegment [constr] StartX=1.15 StartY=4.6 StartZ=0 EndX=3.45 EndY=4.6 EndZ=0
    g34: GeomPoint [constr] X=0 Y=4.6 Z=0
    g35: LineSegment [constr] StartX=-4.93964 StartY=5.1 StartZ=0 EndX=4.93964 EndY=5.1 EndZ=0
    g36: ArcOfCircle [constr] CenterX=0 CenterY=0 CenterZ=0 NormalX=0 NormalY=0 NormalZ=1 AngleXU=0 Radius=7.1 StartAngle=2.34022 EndAngle=7.08456
    g37: GeomPoint [constr] X=0 Y=-7.1 Z=0
    g38: ArcOfCircle [constr] CenterX=0 CenterY=0 CenterZ=0 NormalX=0 NormalY=0 NormalZ=1 AngleXU=0 Radius=7 StartAngle=2.32536 EndAngle=7.09942
    g39: LineSegment [constr] StartX=-4.89898 StartY=5 StartZ=0 EndX=4.89898 EndY=5 EndZ=0
    g40: GeomPoint [constr] X=0 Y=-7 Z=0
  constraints (112):
    c: Coincident(g0,g-1)
    c: Diameter(g0) = 13.2
    c: PointOnObject(g1,g0)
    c: Diameter(g1) = 1
    c: Horizontal(g2)
    c: DistanceY(g0,g2) = 4.6
    c: Coincident(g0,g2)
    c: Coincident(g0,g2)
    c: DistanceY(g1,g0) = 1.2
    c: PointOnObject(g4,g0)
    c: PointOnObject(g5,g0)
    c: PointOnObject(g6,g0)
    c: PointOnObject(g7,g0)
    c: PointOnObject(g3,g0)
    c: PointOnObject(g9,g0)
    c: Equal(g1,g3)
    c: Equal(g3,g4)
    c: Equal(g4,g9)
    c: Equal(g9,g5)
    c: Equal(g5,g6)
    c: Equal(g6,g7)
    c: Equal(g7,g11)
    c: Equal(g11,g12)
    c: Equal(g12,g13)
    c: Equal(g13,g10)
    c: Equal(g10,g8)
    c: PointOnObject(g11,g0)
    c: PointOnObject(g12,g0)
    c: PointOnObject(g13,g0)
    c: PointOnObject(g14,g0)
    c: Coincident(g15,g1)
    c: Coincident(g16,g15)
    c: Coincident(g16,g4)
    c: Coincident(g17,g16)
    c: Coincident(g18,g17)
    c: Coincident(g18,g5)
    c: Coincident(g19,g18)
    c: Coincident(g20,g19)
    c: Coincident(g20,g7)
    c: Coincident(g21,g20)
    c: Coincident(g22,g21)
    c: Coincident(g22,g11)
    c: Coincident(g23,g22)
    c: Coincident(g24,g23)
    c: Coincident(g24,g14)
    c: Coincident(g25,g24)
    c: Coincident(g25,g10)
    c: Coincident(g26,g25)
    c: Coincident(g26,g8)
    c: Coincident(g15,g3)
    c: Coincident(g17,g9)
    c: Coincident(g19,g6)
    c: Coincident(g21,g13)
    c: Coincident(g23,g12)
    c: PointOnObject(g25,g0)
    c: PointOnObject(g26,g0)
    c: Equal(g15,g16)
    c: Equal(g16,g17)
    c: Equal(g17,g18)
    c: Equal(g18,g19)
    c: Equal(g19,g20)
    c: Equal(g20,g21)
    c: Equal(g21,g22)
    c: Equal(g22,g23)
    c: Equal(g23,g24)
    c: Equal(g24,g25)
    c: Equal(g25,g26)
    c: Horizontal(g8,g1)
    c: Equal(g14,g1)
    c: PointOnObject(g27,g2)
    c: Equal(g27,g1)
    c: Coincident(g27,g29)
    c: Coincident(g28,g29)
    c: Distance(g29) = 2.3
    c: Coincident(g28,g31)
    c: Coincident(g30,g31)
    c: Equal(g29,g31)
    c: Parallel(g31,g29)
    c: Coincident(g30,g33)
    c: Coincident(g32,g33)
    c: Equal(g29,g33)
    c: Parallel(g33,g29)
    c: PointOnObject(g34,g-2)
    c: Symmetric(g28,g30,g34)
    c: Equal(g27,g28)
    c: Equal(g28,g30)
    c: Equal(g30,g32)
    c: Horizontal(g33)
    c: Horizontal(g35)
    c: Coincident(g36,g0)
    c: Tangent(g36,g7)
    c: Coincident(g35,g36)
    c: Coincident(g35,g36)
    c: Tangent(g35,g30)
    c: DistanceY(g0,g35) = 5.1
    c: Diameter(g36) = 14.2
    c: PointOnObject(g37,g36)
    c: PointOnObject(g37,g-2)
    c: DistanceY(g37,g35) = 12.2
    c: PointOnObject(g38,g-1)
    c: Diameter(g38) = 14
    c: PointOnObject(g39,g38)
    c: PointOnObject(g39,g38)
    c: Horizontal(g39)
    c: PointOnObject(g38,g-2)
    c: DistanceY(g38,g39) = 5
    c: PointOnObject(g38,g35)
    c: PointOnObject(g38,g35)
    c: DistanceY(g39,g38) = 0.1
    c: PointOnObject(g40,g38)
    c: PointOnObject(g40,g-2)
    c: DistanceY(g37,g40) = 0.1
FEATURE [PartDesign::Pad] Pad002
  BaseFeature = -> Pad
  Direction = (0,0,1)
  Length = 9.5
  Length2 = 10
  Midplane = true
  Profile = -> Sketch002
  ReferenceAxis = -> Sketch002 [N_Axis]
  Refine = true
  Suppressed = false
  Type = 0
FEATURE [Sketcher::SketchObject] Sketch003
  ArcFitTolerance = 0
  AttachmentSupport = -> [XY_Plane]
  FullyConstrained = true
  MakeInternals = false
  MapMode = 5
  sketch-geometry (26):
    g0: ArcOfCircle [constr] CenterX=0 CenterY=0 CenterZ=0 NormalX=0 NormalY=0 NormalZ=1 AngleXU=0 Radius=3.4 StartAngle=2.54863 EndAngle=6.87615
    g1: LineSegment [constr] StartX=-2.81957 StartY=1.9 StartZ=0 EndX=2.81957 EndY=1.9 EndZ=0
    g2: Circle CenterX=-2 CenterY=1.9 CenterZ=0 NormalX=0 NormalY=0 NormalZ=1 AngleXU=0 Radius=0.5
    g3: Circle CenterX=0 CenterY=1.9 CenterZ=0 NormalX=0 NormalY=0 NormalZ=1 AngleXU=0 Radius=0.5
    g4: LineSegment [constr] StartX=-2 StartY=1.9 StartZ=0 EndX=0 EndY=1.9 EndZ=0
    g5: Circle CenterX=2 CenterY=1.9 CenterZ=0 NormalX=0 NormalY=0 NormalZ=1 AngleXU=0 Radius=0.5
    g6: LineSegment [constr] StartX=0 StartY=1.9 StartZ=0 EndX=2 EndY=1.9 EndZ=0
    g7: Circle CenterX=-3.24962 CenterY=1 CenterZ=0 NormalX=0 NormalY=0 NormalZ=1 AngleXU=0 Radius=0.5
    g8: Circle CenterX=-3.22247 CenterY=-1.08429 CenterZ=0 NormalX=0 NormalY=0 NormalZ=1 AngleXU=0 Radius=0.5
    g9: Circle CenterX=-1.98411 CenterY=-2.76103 CenterZ=0 NormalX=0 NormalY=0 NormalZ=1 AngleXU=0 Radius=0.5
    g10: Circle CenterX=0 CenterY=-3.4 CenterZ=0 NormalX=0 NormalY=0 NormalZ=1 AngleXU=0 Radius=0.5
    g11: Circle CenterX=1.98411 CenterY=-2.76103 CenterZ=0 NormalX=0 NormalY=0 NormalZ=1 AngleXU=0 Radius=0.5
    g12: Circle CenterX=3.22247 CenterY=-1.08429 CenterZ=0 NormalX=0 NormalY=0 NormalZ=1 AngleXU=0 Radius=0.5
    g13: Circle CenterX=3.24962 CenterY=1 CenterZ=0 NormalX=0 NormalY=0 NormalZ=1 AngleXU=0 Radius=0.5
    g14: LineSegment [constr] StartX=-3.24962 StartY=1 StartZ=0 EndX=-3.22247 EndY=-1.08429 EndZ=0
    g15: LineSegment [constr] StartX=-3.22247 StartY=-1.08429 StartZ=0 EndX=-1.98411 EndY=-2.76103 EndZ=0
    g16: LineSegment [constr] StartX=-1.98411 StartY=-2.76103 StartZ=0 EndX=0 EndY=-3.4 EndZ=0
    g17: LineSegment [constr] StartX=0 StartY=-3.4 StartZ=0 EndX=1.98411 EndY=-2.76103 EndZ=0
    g18: LineSegment [constr] StartX=1.98411 StartY=-2.76103 StartZ=0 EndX=3.22247 EndY=-1.08429 EndZ=0
    g19: LineSegment [constr] StartX=3.22247 StartY=-1.08429 StartZ=0 EndX=3.24962 EndY=1 EndZ=0
    g20: LineSegment [constr] StartX=-2.53969 StartY=1.4 StartZ=0 EndX=2.53969 EndY=1.4 EndZ=0
    g21: ArcOfCircle [constr] CenterX=0 CenterY=0 CenterZ=0 NormalX=0 NormalY=0 NormalZ=1 AngleXU=0 Radius=2.9 StartAngle=2.63779 EndAngle=6.78699
    g22: ArcOfCircle [constr] CenterX=0 CenterY=0 CenterZ=0 NormalX=0 NormalY=0 NormalZ=1 AngleXU=0 Radius=3 StartAngle=2.61799 EndAngle=6.80678
    g23: LineSegment [constr] StartX=-2.59808 StartY=1.5 StartZ=0 EndX=2.59808 EndY=1.5 EndZ=0
    g24: GeomPoint [constr] X=0 Y=-3 Z=0
    g25: GeomPoint [constr] X=0 Y=-2.9 Z=0
  constraints (73):
    c: Coincident(g0,g-1)
    c: Diameter(g0) = 6.8
    c: Horizontal(g1)
    c: DistanceY(g0,g1) = 1.9
    c: Coincident(g0,g1)
    c: Coincident(g0,g1)
    c: PointOnObject(g2,g1)
    c: Diameter(g2) = 1
    c: Equal(g2,g3) = 1
    c: Coincident(g2,g4)
    c: Coincident(g3,g4)
    c: Distance(g4) = 2
    c: Angle(g4) = 0
    c: Equal(g2,g5) = 1
    c: Coincident(g3,g6)
    c: Coincident(g5,g6)
    c: Equal(g4,g6)
    c: Parallel(g6,g4)
    c: PointOnObject(g3,g-2)
    c: PointOnObject(g7,g0)
    c: PointOnObject(g8,g0)
    c: Equal(g2,g7)
    c: Equal(g7,g8)
    c: Equal(g8,g9)
    c: Equal(g9,g10)
    c: Equal(g10,g11)
    c: Equal(g11,g12)
    c: Equal(g12,g13)
    c: PointOnObject(g9,g0)
    c: PointOnObject(g10,g0)
    c: PointOnObject(g11,g0)
    c: PointOnObject(g12,g0)
    c: PointOnObject(g13,g0)
    c: Coincident(g14,g7)
    c: Coincident(g14,g8)
    c: Coincident(g15,g8)
    c: Coincident(g15,g9)
    c: Coincident(g16,g9)
    c: Coincident(g16,g10)
    c: Coincident(g17,g10)
    c: Coincident(g17,g11)
    c: Coincident(g18,g11)
    c: Coincident(g18,g12)
    c: Coincident(g19,g12)
    c: Coincident(g19,g13)
    c: Equal(g16,g15)
    c: Equal(g15,g14)
    c: Equal(g14,g17)
    c: Equal(g17,g18)
    c: Equal(g18,g19)
    c: DistanceY(g7,g0) = 0.9
    c: Horizontal(g13,g7)
    c: Horizontal(g20)
    c: Tangent(g20,g3)
    c: Coincident(g21,g20)
    c: Diameter(g21) = 5.8
    c: DistanceY(g0,g20) = 1.4
    c: Coincident(g21,g20)
    c: Tangent(g21,g10)
    c: Coincident(g0,g21)
    c: Coincident(g22,g0)
    c: Diameter(g22) = 6
    c: Horizontal(g23)
    c: PointOnObject(g24,g22)
    c: PointOnObject(g24,g-2)
    c: DistanceY(g24,g23) = 4.5
    c: DistanceY(g22,g23) = 1.5
    c: Coincident(g22,g23)
    c: Coincident(g22,g23)
    c: DistanceY(g20,g22) = 0.1
    c: PointOnObject(g25,g21)
    c: PointOnObject(g25,g-2)
    c: DistanceY(g24,g25) = 0.1
FEATURE [PartDesign::Pad] Pad003
  BaseFeature = -> Pad002
  Direction = (0,0,1)
  Length = 9.5
  Length2 = 10
  Midplane = true
  Profile = -> Sketch003
  ReferenceAxis = -> Sketch003 [N_Axis]
  Refine = true
  Suppressed = false
  Type = 0
FEATURE [PartDesign::Plane] DatumPlane001
  AttachmentOffset = pos=(0,0,-4.75) rot=(0,0,1;0rad)
  AttachmentSupport = -> [XY_Plane]
  Length = 60
  MapMode = 5
  Placement = pos=(0,0,-4.75) rot=(0,0,1;0rad)
  ResizeMode = 0
  Width = 60
FEATURE [PartDesign::Plane] DatumPlane
  AttachmentOffset = pos=(0,0,-1.55) rot=(0,0,1;0rad)
  AttachmentSupport = -> [XY_Plane001]
  Length = 60
  MapMode = 5
  Placement = pos=(0,0,-1.55) rot=(0,0,1;0rad)
  ResizeMode = 0
  Width = 60
FEATURE [Sketcher::SketchObject] Sketch006
  ArcFitTolerance = 0
  AttachmentSupport = -> [DatumPlane]
  FullyConstrained = true
  MakeInternals = false
  MapMode = 5
  Placement = pos=(0,0,-1.55) rot=(0,0,1;0rad)
  sketch-geometry (2):
    g0: ArcOfCircle CenterX=0 CenterY=0 CenterZ=0 NormalX=0 NormalY=0 NormalZ=1 AngleXU=0 Radius=3.9 StartAngle=2.47872 EndAngle=6.94606
    g1: LineSegment StartX=-3.07409 StartY=2.4 StartZ=0 EndX=3.07409 EndY=2.4 EndZ=0
  constraints (6):
    c: Coincident(g0,g-1)
    c: Horizontal(g1)
    c: Diameter(g0) = 7.8
    c: DistanceY(g-1,g1) = 2.4
    c: Coincident(g0,g1)
    c: Coincident(g0,g1)
FEATURE [PartDesign::Pad] Pad004
  Direction = (0,0,1)
  Length = 10
  Length2 = 10
  Placement = pos=(0,0,-1.55) rot=(0,0,1;0rad)
  Profile = -> Sketch006
  ReferenceAxis = -> Sketch006 [N_Axis]
  Reversed = true
  Suppressed = false
  Type = 0
FEATURE [Sketcher::SketchObject] Sketch007
  ArcFitTolerance = 0
  AttachmentSupport = -> [YZ_Plane001]
  FullyConstrained = true
  MakeInternals = false
  MapMode = 5
  Placement = pos=(0,0,0) rot=(0.57735,0.57735,0.57735;2.0944rad)
  sketch-geometry (5):
    g0: LineSegment StartX=-1 StartY=-8 StartZ=0 EndX=-1 EndY=8 EndZ=0
    g1: LineSegment StartX=-1 StartY=8 StartZ=0 EndX=1 EndY=8 EndZ=0
    g2: LineSegment StartX=1 StartY=8 StartZ=0 EndX=1 EndY=-8 EndZ=0
    g3: LineSegment StartX=1 StartY=-8 StartZ=0 EndX=-1 EndY=-8 EndZ=0
    g4: GeomPoint [constr] X=0 Y=0 Z=0
  constraints (12):
    c: Coincident(g0,g1)
    c: Coincident(g1,g2)
    c: Coincident(g2,g3)
    c: Coincident(g3,g0)
    c: Horizontal(g1)
    c: Horizontal(g3)
    c: Vertical(g0)
    c: Vertical(g2)
    c: Symmetric(g1,g0,g4)
    c: Coincident(g4,g-1)
    c: DistanceY(g2,g2) = 16
    c: DistanceX(g1,g1) = 2
FEATURE [PartDesign::Pad] Pad005
  BaseFeature = -> Pad004
  Direction = (1,0,0)
  Length = 2
  Length2 = 10
  Midplane = true
  Placement = pos=(0,0,-1.55) rot=(0,0,1;0rad)
  Profile = -> Sketch007
  ReferenceAxis = -> Sketch007 [N_Axis]
  Suppressed = false
  Type = 0
FEATURE [PartDesign::Plane] DatumPlane002
  AttachmentOffset = pos=(0,0,2.25) rot=(0,0,1;0rad)
  AttachmentSupport = -> [XY_Plane002]
  Length = 60
  MapMode = 5
  Placement = pos=(0,0,2.25) rot=(0,0,1;0rad)
  ResizeMode = 0
  Width = 60
FEATURE [Sketcher::SketchObject] Sketch008
  ArcFitTolerance = 0
  AttachmentSupport = -> [DatumPlane002]
  FullyConstrained = true
  MakeInternals = false
  MapMode = 5
  Placement = pos=(0,0,2.25) rot=(0,0,1;0rad)
  sketch-geometry (3):
    g0: ArcOfCircle CenterX=0 CenterY=0 CenterZ=0 NormalX=0 NormalY=0 NormalZ=1 AngleXU=0 Radius=6.1 StartAngle=2.40451 EndAngle=7.02027
    g1: LineSegment StartX=-4.51664 StartY=4.1 StartZ=0 EndX=4.51664 EndY=4.1 EndZ=0
    g2: Circle CenterX=0 CenterY=0 CenterZ=0 NormalX=0 NormalY=0 NormalZ=1 AngleXU=0 Radius=10
  constraints (8):
    c: Coincident(g0,g-1)
    c: Horizontal(g1)
    c: Diameter(g0) = 12.2
    c: DistanceY(g-1,g1) = 4.1
    c: Coincident(g0,g1)
    c: Coincident(g0,g1)
    c: Coincident(g0,g2)
    c: Diameter(g2) = 20
FEATURE [PartDesign::Pad] Pad006
  Direction = (0,0,1)
  Length = 10
  Length2 = 10
  Placement = pos=(0,0,2.25) rot=(0,0,1;0rad)
  Profile = -> Sketch008
  ReferenceAxis = -> Sketch008 [N_Axis]
  Suppressed = false
  Type = 0
FEATURE [Sketcher::SketchObject] Sketch009
  ArcFitTolerance = 0
  AttachmentSupport = -> [YZ_Plane002]
  FullyConstrained = true
  MakeInternals = false
  MapMode = 5
  Placement = pos=(0,0,0) rot=(0.57735,0.57735,0.57735;2.0944rad)
  sketch-geometry (5):
    g0: LineSegment StartX=6 StartY=-5 StartZ=0 EndX=6 EndY=5 EndZ=0
    g1: LineSegment StartX=6 StartY=5 StartZ=0 EndX=8 EndY=5 EndZ=0
    g2: LineSegment StartX=8 StartY=5 StartZ=0 EndX=8 EndY=-5 EndZ=0
    g3: LineSegment StartX=8 StartY=-5 StartZ=0 EndX=6 EndY=-5 EndZ=0
    g4: GeomPoint [constr] X=7 Y=0 Z=0
  constraints (13):
    c: Coincident(g0,g1)
    c: Coincident(g1,g2)
    c: Coincident(g2,g3)
    c: Coincident(g3,g0)
    c: Horizontal(g1)
    c: Horizontal(g3)
    c: Vertical(g0)
    c: Vertical(g2)
    c: Symmetric(g1,g0,g4)
    c: PointOnObject(g4,g-1)
    c: DistanceY(g2,g2) = 10
    c: DistanceX(g1,g1) = 2
    c: DistanceX(g-1,g0) = 6
FEATURE [PartDesign::Pad] Pad007
  BaseFeature = -> Pad006
  Direction = (1,0,0)
  Length = 2
  Length2 = 10
  Midplane = true
  Placement = pos=(0,0,2.25) rot=(0,0,1;0rad)
  Profile = -> Sketch009
  ReferenceAxis = -> Sketch009 [N_Axis]
  Suppressed = false
  Type = 0
FEATURE [Sketcher::SketchObject] Sketch010
  ArcFitTolerance = 0
  AttachmentSupport = -> [DatumPlane001]
  FullyConstrained = true
  MakeInternals = false
  MapMode = 5
  Placement = pos=(0,0,-4.75) rot=(0,0,1;0rad)
  sketch-geometry (4):
    g0: ArcOfCircle CenterX=0 CenterY=0 CenterZ=0 NormalX=0 NormalY=0 NormalZ=1 AngleXU=0 Radius=5 StartAngle=2.49809 EndAngle=6.92669
    g1: LineSegment StartX=-4 StartY=3 StartZ=0 EndX=-4 EndY=5.5 EndZ=0
    g2: LineSegment StartX=-4 StartY=5.5 StartZ=0 EndX=4 EndY=5.5 EndZ=0
    g3: LineSegment StartX=4 StartY=5.5 StartZ=0 EndX=4 EndY=3 EndZ=0
  constraints (11):
    c: Coincident(g0,g-1)
    c: Diameter(g0) = 10
    c: Coincident(g2,g1)
    c: Coincident(g3,g2)
    c: Vertical(g3)
    c: Vertical(g1)
    c: Symmetric(g1,g2,g-2)
    c: DistanceX(g2,g2) = 8
    c: DistanceY(g3,g3) = 2.5
    c: Coincident(g0,g3)
    c: Coincident(g0,g1)
FEATURE [PartDesign::Pocket] Pocket
  BaseFeature = -> Pad003
  Direction = (0,0,-1)
  Length = 2.2
  Length2 = 5
  Profile = -> Sketch010
  ReferenceAxis = -> Sketch010 [N_Axis]
  Reversed = true
  Suppressed = false
  Type = 0
FEATURE [PartDesign::Plane] DatumPlane003
  AttachmentOffset = pos=(0,0,3.75) rot=(0,0,1;0rad)
  AttachmentSupport = -> [XY_Plane001]
  Length = 60
  MapMode = 5
  Placement = pos=(0,0,3.75) rot=(0,0,1;0rad)
  ResizeMode = 0
  Width = 60
FEATURE [Sketcher::SketchObject] Sketch011
  ArcFitTolerance = 0
  AttachmentSupport = -> [DatumPlane003]
  FullyConstrained = true
  MakeInternals = false
  MapMode = 5
  Placement = pos=(0,0,3.75) rot=(0,0,1;0rad)
  sketch-geometry (2):
    g0: ArcOfCircle CenterX=0 CenterY=0 CenterZ=0 NormalX=0 NormalY=0 NormalZ=1 AngleXU=0 Radius=3.88 StartAngle=2.48123 EndAngle=6.94355
    g1: LineSegment StartX=-3.06431 StartY=2.38 StartZ=0 EndX=3.06431 EndY=2.38 EndZ=0
  constraints (6):
    c: Coincident(g0,g-1)
    c: Horizontal(g1)
    c: Coincident(g0,g1)
    c: Coincident(g0,g1)
    c: Diameter(g0) = 7.76
    c: DistanceY(g0,g0) = 2.38
FEATURE [PartDesign::Pad] Pad008
  BaseFeature = -> Pad005
  Direction = (0,0,1)
  Length = 10
  Length2 = 10
  Placement = pos=(0,0,-1.55) rot=(0,0,1;0rad)
  Profile = -> Sketch011
  ReferenceAxis = -> Sketch011 [N_Axis]
  Suppressed = false
  Type = 0
FEATURE [PartDesign::Chamfer] Chamfer
  Angle = 45
  Base = -> Pad008 [Edge19,Edge20,Edge3,Edge5]
  BaseFeature = -> Pad008
  ChamferType = 0
  FlipDirection = false
  Placement = pos=(0,0,-1.55) rot=(0,0,1;0rad)
  Size = 1
  Size2 = 1
  SupportTransform = false
  Suppressed = false
  UseAllEdges = false
FEATURE [PartDesign::Body] Body001
  AllowCompound = false
  Group = -> [DatumPlane,Sketch006,Pad004,Sketch007,Pad005,DatumPlane003,Sketch011,Pad008,Chamfer]
  Origin = -> Origin001
  Tip = -> Chamfer
FEATURE [PartDesign::Boolean] Boolean
  BaseFeature = -> Pocket
  Group = -> [Body001]
  Suppressed = false
  Type = 1
  UsePlacement = false
FEATURE [PartDesign::Plane] DatumPlane004
  AttachmentOffset = pos=(0,0,-3.75) rot=(0,0,1;0rad)
  AttachmentSupport = -> [XY_Plane002]
  Length = 60
  MapMode = 5
  Placement = pos=(0,0,-3.75) rot=(0,0,1;0rad)
  ResizeMode = 0
  Width = 60
FEATURE [Sketcher::SketchObject] Sketch012
  ArcFitTolerance = 0
  AttachmentSupport = -> [DatumPlane004]
  FullyConstrained = true
  MakeInternals = false
  MapMode = 5
  Placement = pos=(0,0,-3.75) rot=(0,0,1;0rad)
  sketch-geometry (3):
    g0: ArcOfCircle CenterX=0 CenterY=0 CenterZ=0 NormalX=0 NormalY=0 NormalZ=1 AngleXU=0 Radius=6.1 StartAngle=2.40451 EndAngle=7.02027
    g1: Circle CenterX=0 CenterY=0 CenterZ=0 NormalX=0 NormalY=0 NormalZ=1 AngleXU=0 Radius=10
    g2: LineSegment StartX=-4.51664 StartY=4.1 StartZ=0 EndX=4.51664 EndY=4.1 EndZ=0
  constraints (8):
    c: Coincident(g0,g-1)
    c: Coincident(g1,g0)
    c: Horizontal(g2)
    c: DistanceY(g0,g2) = 4.1
    c: Diameter(g0) = 12.2
    c: Diameter(g1) = 20
    c: Coincident(g0,g2)
    c: Coincident(g0,g2)
FEATURE [PartDesign::Pad] Pad009
  BaseFeature = -> Pad007
  Direction = (0,0,1)
  Length = 10
  Length2 = 10
  Placement = pos=(0,0,2.25) rot=(0,0,1;0rad)
  Profile = -> Sketch012
  ReferenceAxis = -> Sketch012 [N_Axis]
  Reversed = true
  Suppressed = false
  Type = 0
FEATURE [PartDesign::Chamfer] Chamfer001
  Angle = 45
  Base = -> Pad009 [Edge24,Edge23]
  BaseFeature = -> Pad009
  ChamferType = 0
  FlipDirection = false
  Placement = pos=(0,0,2.25) rot=(0,0,1;0rad)
  Size = 1
  Size2 = 1
  SupportTransform = false
  Suppressed = false
  UseAllEdges = false
FEATURE [PartDesign::Chamfer] Chamfer002
  Angle = 70
  Base = -> Chamfer001 [Edge27,Edge28]
  BaseFeature = -> Chamfer001
  ChamferType = 2
  FlipDirection = false
  Placement = pos=(0,0,2.25) rot=(0,0,1;0rad)
  Size = 1
  Size2 = 3
  SupportTransform = false
  Suppressed = false
  UseAllEdges = false
FEATURE [PartDesign::Body] Body002
  AllowCompound = false
  Group = -> [DatumPlane002,Sketch008,Pad006,Sketch009,Pad007,DatumPlane004,Sketch012,Pad009,Chamfer001,Chamfer002]
  Origin = -> Origin002
  Tip = -> Chamfer002
FEATURE [PartDesign::Boolean] Boolean001
  BaseFeature = -> Boolean
  Group = -> [Body002]
  Suppressed = false
  Type = 1
  UsePlacement = false
FEATURE [PartDesign::CoordinateSystem] LCS_1
  AttacherType = Attacher::AttachEngine3D
  AttachmentOffset = pos=(0,0,0) rot=(0,0,-1;2.47837rad)
  AttachmentSupport = -> [Boolean001]
  MapMode = 11
  Placement = pos=(-4e-16,0,4.75) rot=(0,0,1;1.57366rad)
FEATURE [PartDesign::CoordinateSystem] LCS_2
  AttacherType = Attacher::AttachEngine3D
  AttachmentOffset = pos=(0,0,0) rot=(0,0,-1;2.47837rad)
  AttachmentSupport = -> [Boolean001]
  MapMode = 11
  Placement = pos=(-4e-16,0,-2.55) rot=(0,0,1;1.57115rad)
FEATURE [PartDesign::CoordinateSystem] LCS_3
  AttacherType = Attacher::AttachEngine3D
  AttachmentSupport = -> [Boolean001]
  MapMode = 5
  Placement = pos=(0,0,-4.75) rot=(1,0,0;3.14159rad)
FEATURE [PartDesign::Body] Body  label="PLASTIC-TEK2-KNOB-INTERFACE"
  AllowCompound = false
  Group = -> [Sketch,Pad,Pad002,Sketch002,Sketch003,Pad003,DatumPlane001,Pocket,Sketch010,Boolean,Boolean001,LCS_1,LCS_2,LCS_3]
  Origin = -> Origin
  Tip = -> Boolean001
---- part ../Design/SCREW-M1.6x5-C/SCREW-M1.6x5-C.FCStd = doc fcstd_20a1a2ffa229 ----
FCSTD DOCUMENT  (FreeCAD 1.0R39319 (Git))
Label: SCREW-M1.6x5-C
License: All rights reserved
LicenseURL: https://en.wikipedia.org/wiki/All_rights_reserved
objects: Sketcher::SketchObject×3, PartDesign::Revolution×1, PartDesign::Pocket×1, PartDesign::Fillet×1, PartDesign::AdditiveHelix×1, PartDesign::Line×1, PartDesign::Body×1
note: 20 computed .brp shape members not serialized (recipe doc carries the construction recipe); baked Part::Feature solids carry a one-line shape summary decoded from their .brp

FEATURE [Sketcher::SketchObject] Sketch  label="Profile"
  ArcFitTolerance = 0
  AttachmentSupport = -> [XZ_Plane]
  FullyConstrained = true
  MakeInternals = false
  MapMode = 5
  Placement = pos=(0,0,0) rot=(1,0,0;1.5708rad)
  expr: .Constraints.R = 0.61 mm
  sketch-geometry (7):
    g0: LineSegment StartX=0 StartY=0.8 StartZ=0 EndX=0 EndY=-4.9 EndZ=0
    g1: LineSegment StartX=-1.4 StartY=0.79 StartZ=0 EndX=-0.61 EndY=0 EndZ=0
    g2: LineSegment StartX=-0.61 StartY=0 StartZ=0 EndX=-0.61 EndY=-4.9 EndZ=0
    g3: LineSegment StartX=0 StartY=-4.9 StartZ=0 EndX=-0.61 EndY=-4.9 EndZ=0
    g4: LineSegment StartX=-1.4 StartY=0.79 StartZ=0 EndX=-1.4 EndY=0.79 EndZ=0
    g5: LineSegment StartX=-1.4 StartY=0.79 StartZ=0 EndX=-1.4 EndY=0.8 EndZ=0
    g6: LineSegment StartX=-1.4 StartY=0.8 StartZ=0 EndX=0 EndY=0.8 EndZ=0
  constraints (21):
    c: PointOnObject(g0,g-2)
    c: Coincident(g2,g1)
    c: Vertical(g2)
    c: Coincident(g3,g0)
    c: Horizontal(g3)
    c: Coincident(g2,g3)
    c: DistanceX(g3,g3) = 0.61  'R'
    c: Distance(g2) = 4.9  'L'
    c: DistanceY(g1,g0) = 0.8
    c: Coincident(g4,g1)
    c: PointOnObject(g0,g-2)
    c: PointOnObject(g1,g-1)
    c: DistanceX(g4,g-1) = 1.4
    c: DistanceY(g-1,g4) = 0.79
    c: Vertical(g4)
    c: Angle(g1,g2) = 2.35619
    c: Coincident(g5,g4)
    c: Vertical(g5)
    c: Coincident(g6,g5)
    c: Coincident(g6,g0)
    c: Horizontal(g6)
FEATURE [PartDesign::Revolution] Revolution
  Angle = 360
  Angle2 = 60
  Axis = (0,2e-16,1)
  Base = (0,0,0)
  Placement = pos=(0,0,0) rot=(1,0,0;1.5708rad)
  Profile = -> Sketch
  ReferenceAxis = -> Sketch [V_Axis]
  Suppressed = false
  Type = 0
FEATURE [Sketcher::SketchObject] Sketch001
  ArcFitTolerance = 0
  AttachmentSupport = -> [XZ_Plane]
  FullyConstrained = true
  MakeInternals = false
  MapMode = 5
  Placement = pos=(0,0,0) rot=(1,0,0;1.5708rad)
  expr: Constraints[23] = <<Profile>>.Constraints.L
  expr: Constraints[24] = <<Profile>>.Constraints.R
  sketch-geometry (9):
    g0: LineSegment StartX=-0.61 StartY=-4.9 StartZ=0 EndX=-0.7905 EndY=-4.79579 EndZ=0
    g1: LineSegment StartX=-0.7905 StartY=-4.79579 StartZ=0 EndX=-0.61 EndY=-4.69158 EndZ=0
    g2: LineSegment [constr] StartX=-0.61 StartY=-4.69158 StartZ=0 EndX=0 EndY=-4.69158 EndZ=0
    g3: LineSegment [constr] StartX=0 StartY=-4.69158 StartZ=0 EndX=0 EndY=-4.9 EndZ=0
    g4: LineSegment [constr] StartX=-0.61 StartY=-4.9 StartZ=0 EndX=0 EndY=-4.9 EndZ=0
    g5: LineSegment [constr] StartX=-0.61 StartY=-4.69158 StartZ=0 EndX=-0.61 EndY=-4.9 EndZ=0
    g6: LineSegment StartX=-0.61 StartY=-4.69158 StartZ=0 EndX=-0.56 EndY=-4.69158 EndZ=0
    g7: LineSegment StartX=-0.56 StartY=-4.69158 StartZ=0 EndX=-0.56 EndY=-4.9 EndZ=0
    g8: LineSegment StartX=-0.56 StartY=-4.9 StartZ=0 EndX=-0.61 EndY=-4.9 EndZ=0
  constraints (26):
    c: Angle(g0,g1) = 1.0472
    c: Equal(g1,g0)
    c: Coincident(g0,g1)
    c: Coincident(g2,g1)
    c: Horizontal(g2)
    c: Coincident(g3,g2)
    c: Vertical(g1,g0)
    c: Vertical(g3)
    c: DistanceX(g0,g2) = 0.7905
    c: Coincident(g4,g0)
    c: Coincident(g4,g3)
    c: Coincident(g5,g1)
    c: Coincident(g5,g0)
    c: Coincident(g6,g1)
    c: PointOnObject(g6,g2)
    c: Coincident(g7,g6)
    c: PointOnObject(g7,g4)
    c: Vertical(g7)
    c: Coincident(g8,g7)
    c: Coincident(g8,g0)
    c: DistanceX(g6,g6) = 0.05
    c: PointOnObject(g3,g-2)
    c: Horizontal(g4)
    c: DistanceY(g3,g-1) = 4.9
    c: DistanceX(g0,g3) = 0.61
    c: DistanceY(g0,g1) = 0.104212
FEATURE [Sketcher::SketchObject] Sketch002
  ArcFitTolerance = 0
  FullyConstrained = true
  MakeInternals = false
  MapMode = 5
  Placement = pos=(-1e-16,2.1e-15,0.5) rot=(0.707107,0.707107,0;3.14159rad)
  sketch-geometry (14):
    g0: LineSegment StartX=-0.25 StartY=-0.8 StartZ=0 EndX=-0.25 EndY=-0.25 EndZ=0
    g1: LineSegment StartX=-0.25 StartY=0.8 StartZ=0 EndX=0.25 EndY=0.8 EndZ=0
    g2: LineSegment StartX=0.25 StartY=0.8 StartZ=0 EndX=0.25 EndY=0.25 EndZ=0
    g3: LineSegment StartX=0.25 StartY=-0.8 StartZ=0 EndX=-0.25 EndY=-0.8 EndZ=0
    g4: GeomPoint [constr] X=0 Y=0 Z=0
    g5: LineSegment StartX=-0.8 StartY=0.25 StartZ=0 EndX=-0.8 EndY=-0.25 EndZ=0
    g6: LineSegment StartX=-0.8 StartY=-0.25 StartZ=0 EndX=-0.25 EndY=-0.25 EndZ=0
    g7: LineSegment StartX=0.8 StartY=-0.25 StartZ=0 EndX=0.8 EndY=0.25 EndZ=0
    g8: LineSegment StartX=0.8 StartY=0.25 StartZ=0 EndX=0.25 EndY=0.25 EndZ=0
    g9: GeomPoint [constr] X=0 Y=0 Z=0
    g10: LineSegment StartX=-0.25 StartY=0.25 StartZ=0 EndX=-0.25 EndY=0.8 EndZ=0
    g11: LineSegment StartX=0.25 StartY=-0.25 StartZ=0 EndX=0.8 EndY=-0.25 EndZ=0
    g12: LineSegment StartX=-0.25 StartY=0.25 StartZ=0 EndX=-0.8 EndY=0.25 EndZ=0
    g13: LineSegment StartX=0.25 StartY=-0.25 StartZ=0 EndX=0.25 EndY=-0.8 EndZ=0
  constraints (36):
    c: Coincident(g10,g1)
    c: Coincident(g1,g2)
    c: Coincident(g13,g3)
    c: Coincident(g3,g0)
    c: Horizontal(g1)
    c: Horizontal(g3)
    c: Vertical(g0)
    c: Vertical(g2)
    c: Symmetric(g1,g0,g4)
    c: Coincident(g4,g-1)
    c: Coincident(g5,g6)
    c: Coincident(g11,g7)
    c: Coincident(g7,g8)
    c: Coincident(g12,g5)
    c: Horizontal(g6)
    c: Horizontal(g8)
    c: Vertical(g5)
    c: Vertical(g7)
    c: Symmetric(g11,g5,g9)
    c: Coincident(g9,g4)
    c: Distance(g1) = 0.5
    c: Distance(g7) = 0.5
    c: Coincident(g6,g0)
    c: Vertical(g10)
    c: Vertical(g10,g0)
    c: Coincident(g12,g10)
    c: Coincident(g2,g8)
    c: Coincident(g13,g11)
    c: Horizontal(g12)
    c: DistanceX(g5,g7) = 1.6
    c: Vertical(g13)
    c: DistanceY(g3,g1) = 1.6
    c: Horizontal(g11)
    c: Horizontal(g2,g10)
    c: Horizontal(g11,g0)
    c: Vertical(g2,g11)
FEATURE [PartDesign::Pocket] Pocket
  BaseFeature = -> Revolution
  Direction = (-1e-16,1e-16,1)
  Length = 1
  Length2 = 5
  Placement = pos=(0,0,0) rot=(1,0,0;1.5708rad)
  Profile = -> Sketch002
  ReferenceAxis = -> Sketch002 [N_Axis]
  Refine = true
  Suppressed = false
  Type = 1
FEATURE [PartDesign::Fillet] Fillet
  Base = -> Pocket [Edge24,Edge30,Edge42,Edge36]
  BaseFeature = -> Pocket
  Placement = pos=(0,0,0) rot=(1,0,0;1.5708rad)
  Radius = 0.1
  Refine = true
  SupportTransform = false
  Suppressed = false
  UseAllEdges = false
FEATURE [PartDesign::AdditiveHelix] AdditiveHelix
  Angle = 0
  Axis = (0,2e-16,1)
  Base = (0,0,0)
  BaseFeature = -> Fillet
  Growth = 0
  HasBeenEdited = true
  Height = 4.9
  LeftHanded = false
  Mode = 0
  Outside = false
  Pitch = 0.35
  Placement = pos=(0,0,0) rot=(1,0,0;1.5708rad)
  Profile = -> Sketch001
  ReferenceAxis = -> Sketch001 [V_Axis]
  Suppressed = false
  Tolerance = 0.1
  Turns = 14
  expr: Height = <<Profile>>.Constraints.L - 1 mm + 1 mm
FEATURE [PartDesign::Line] CircleAxis_1
  AttacherType = Attacher::AttachEngineLine
  AttachmentSupport = -> [AdditiveHelix]
  Length = 7.9196
  MapMode = 19
  Placement = pos=(0,4e-16,0.8) rot=(0,0,1;3.14159rad)
  ResizeMode = 1
FEATURE [PartDesign::Body] Body  label="SCREW-M1.6x5-C"
  AllowCompound = false
  Group = -> [Sketch,Revolution,Pocket,Fillet,Sketch001,AdditiveHelix,Sketch002,CircleAxis_1]
  Origin = -> Origin
  Tip = -> AdditiveHelix
---- part ../Design/SCREW-M1.6x8/SCREW-M1.6x8.FCStd = doc fcstd_10ca11216a0e ----
FCSTD DOCUMENT  (FreeCAD 1.0R39319 (Git))
Label: SCREW-M1.6x8
License: All rights reserved
LicenseURL: https://en.wikipedia.org/wiki/All_rights_reserved
objects: Sketcher::SketchObject×3, PartDesign::Revolution×1, PartDesign::Pocket×1, PartDesign::Fillet×1, PartDesign::AdditiveHelix×1, PartDesign::CoordinateSystem×1, PartDesign::Body×1
note: 20 computed .brp shape members not serialized (recipe doc carries the construction recipe); baked Part::Feature solids carry a one-line shape summary decoded from their .brp

FEATURE [Sketcher::SketchObject] Sketch  label="Profile"
  ArcFitTolerance = 0
  AttachmentSupport = -> [XZ_Plane]
  FullyConstrained = true
  MakeInternals = false
  MapMode = 5
  Placement = pos=(0,0,0) rot=(1,0,0;1.5708rad)
  sketch-geometry (6):
    g0: LineSegment StartX=0 StartY=1.3 StartZ=0 EndX=0 EndY=-8 EndZ=0
    g1: LineSegment StartX=-1.6 StartY=0 StartZ=0 EndX=-0.6105 EndY=0 EndZ=0
    g2: LineSegment StartX=-0.6105 StartY=0 StartZ=0 EndX=-0.6105 EndY=-8 EndZ=0
    g3: LineSegment StartX=0 StartY=-8 StartZ=0 EndX=-0.6105 EndY=-8 EndZ=0
    g4: LineSegment StartX=-1.6 StartY=0 StartZ=0 EndX=-1.6 EndY=0.5 EndZ=0
    g5: ArcOfCircle CenterX=0 CenterY=-0.7 CenterZ=0 NormalX=0 NormalY=0 NormalZ=1 AngleXU=0 Radius=2 StartAngle=1.5708 EndAngle=2.49809
  constraints (19):
    c: PointOnObject(g0,g-2)
    c: Horizontal(g1)
    c: Coincident(g2,g1)
    c: Vertical(g2)
    c: Coincident(g3,g0)
    c: Horizontal(g3)
    c: Coincident(g2,g3)
    c: DistanceX(g3,g3) = 0.6105
    c: Distance(g2) = 8  'L'
    c: DistanceY(g1,g0) = 1.3
    c: Distance(g1,g0) = 1.6
    c: Coincident(g4,g1)
    c: Vertical(g4)
    c: PointOnObject(g5,g0)
    c: Coincident(g5,g0)
    c: Coincident(g5,g4)
    c: DistanceY(g4,g4) = 0.5
    c: PointOnObject(g0,g-2)
    c: PointOnObject(g1,g-1)
FEATURE [PartDesign::Revolution] Revolution
  Angle = 360
  Angle2 = 60
  Axis = (0,2e-16,1)
  Base = (0,0,0)
  Placement = pos=(0,0,0) rot=(1,0,0;1.5708rad)
  Profile = -> Sketch
  ReferenceAxis = -> Sketch [V_Axis]
  Suppressed = false
  Type = 0
FEATURE [Sketcher::SketchObject] Sketch001
  ArcFitTolerance = 0
  AttachmentSupport = -> [XZ_Plane]
  ExternalGeometry = -> [Revolution]
  FullyConstrained = true
  MakeInternals = false
  MapMode = 5
  Placement = pos=(0,0,0) rot=(1,0,0;1.5708rad)
  sketch-geometry (9):
    g0: LineSegment StartX=-0.6105 StartY=-8 StartZ=0 EndX=-0.7905 EndY=-7.89608 EndZ=0
    g1: LineSegment StartX=-0.7905 StartY=-7.89608 StartZ=0 EndX=-0.6105 EndY=-7.79215 EndZ=0
    g2: LineSegment [constr] StartX=-0.6105 StartY=-7.79215 StartZ=0 EndX=0 EndY=-7.79215 EndZ=0
    g3: LineSegment [constr] StartX=0 StartY=-7.79215 StartZ=0 EndX=0 EndY=-8 EndZ=0
    g4: LineSegment [constr] StartX=-0.6105 StartY=-8 StartZ=0 EndX=0 EndY=-8 EndZ=0
    g5: LineSegment [constr] StartX=-0.6105 StartY=-7.79215 StartZ=0 EndX=-0.6105 EndY=-8 EndZ=0
    g6: LineSegment StartX=-0.6105 StartY=-7.79215 StartZ=0 EndX=-0.5605 EndY=-7.79215 EndZ=0
    g7: LineSegment StartX=-0.5605 StartY=-7.79215 StartZ=0 EndX=-0.5605 EndY=-8 EndZ=0
    g8: LineSegment StartX=-0.5605 StartY=-8 StartZ=0 EndX=-0.6105 EndY=-8 EndZ=0
  constraints (23):
    c: Angle(g0,g1) = 1.0472
    c: Equal(g1,g0)
    c: Coincident(g0,g1)
    c: Coincident(g2,g1)
    c: Horizontal(g2)
    c: Coincident(g3,g2)
    c: Coincident(g0,g-3)
    c: Vertical(g1,g0)
    c: Vertical(g3)
    c: DistanceX(g0,g2) = 0.7905
    c: Symmetric(g0,g-3,g3)
    c: Coincident(g4,g0)
    c: Coincident(g4,g3)
    c: Coincident(g5,g1)
    c: Coincident(g5,g0)
    c: Coincident(g6,g1)
    c: PointOnObject(g6,g2)
    c: Coincident(g7,g6)
    c: PointOnObject(g7,g4)
    c: Vertical(g7)
    c: Coincident(g8,g7)
    c: Coincident(g8,g0)
    c: DistanceX(g6,g6) = 0.05
FEATURE [Sketcher::SketchObject] Sketch002
  ArcFitTolerance = 0
  FullyConstrained = true
  MakeInternals = false
  MapMode = 5
  Placement = pos=(-1e-16,2.1e-15,0.5) rot=(0.707107,0.707107,0;3.14159rad)
  sketch-geometry (14):
    g0: LineSegment StartX=-0.25 StartY=-0.8 StartZ=0 EndX=-0.25 EndY=-0.25 EndZ=0
    g1: LineSegment StartX=-0.25 StartY=0.8 StartZ=0 EndX=0.25 EndY=0.8 EndZ=0
    g2: LineSegment StartX=0.25 StartY=0.8 StartZ=0 EndX=0.25 EndY=0.25 EndZ=0
    g3: LineSegment StartX=0.25 StartY=-0.8 StartZ=0 EndX=-0.25 EndY=-0.8 EndZ=0
    g4: GeomPoint [constr] X=0 Y=0 Z=0
    g5: LineSegment StartX=-0.8 StartY=0.25 StartZ=0 EndX=-0.8 EndY=-0.25 EndZ=0
    g6: LineSegment StartX=-0.8 StartY=-0.25 StartZ=0 EndX=-0.25 EndY=-0.25 EndZ=0
    g7: LineSegment StartX=0.8 StartY=-0.25 StartZ=0 EndX=0.8 EndY=0.25 EndZ=0
    g8: LineSegment StartX=0.8 StartY=0.25 StartZ=0 EndX=0.25 EndY=0.25 EndZ=0
    g9: GeomPoint [constr] X=0 Y=0 Z=0
    g10: LineSegment StartX=-0.25 StartY=0.25 StartZ=0 EndX=-0.25 EndY=0.8 EndZ=0
    g11: LineSegment StartX=0.25 StartY=-0.25 StartZ=0 EndX=0.8 EndY=-0.25 EndZ=0
    g12: LineSegment StartX=-0.25 StartY=0.25 StartZ=0 EndX=-0.8 EndY=0.25 EndZ=0
    g13: LineSegment StartX=0.25 StartY=-0.25 StartZ=0 EndX=0.25 EndY=-0.8 EndZ=0
  constraints (36):
    c: Coincident(g10,g1)
    c: Coincident(g1,g2)
    c: Coincident(g13,g3)
    c: Coincident(g3,g0)
    c: Horizontal(g1)
    c: Horizontal(g3)
    c: Vertical(g0)
    c: Vertical(g2)
    c: Symmetric(g1,g0,g4)
    c: Coincident(g4,g-1)
    c: Coincident(g5,g6)
    c: Coincident(g11,g7)
    c: Coincident(g7,g8)
    c: Coincident(g12,g5)
    c: Horizontal(g6)
    c: Horizontal(g8)
    c: Vertical(g5)
    c: Vertical(g7)
    c: Symmetric(g11,g5,g9)
    c: Coincident(g9,g4)
    c: Distance(g1) = 0.5
    c: Distance(g7) = 0.5
    c: Coincident(g6,g0)
    c: Vertical(g10)
    c: Vertical(g10,g0)
    c: Coincident(g12,g10)
    c: Coincident(g2,g8)
    c: Coincident(g13,g11)
    c: Horizontal(g12)
    c: DistanceX(g5,g7) = 1.6
    c: Vertical(g13)
    c: DistanceY(g3,g1) = 1.6
    c: Horizontal(g11)
    c: Horizontal(g2,g10)
    c: Horizontal(g11,g0)
    c: Vertical(g2,g11)
FEATURE [PartDesign::Pocket] Pocket
  BaseFeature = -> Revolution
  Direction = (-1e-16,1e-16,1)
  Length = 1
  Length2 = 5
  Placement = pos=(0,0,0) rot=(1,0,0;1.5708rad)
  Profile = -> Sketch002
  ReferenceAxis = -> Sketch002 [N_Axis]
  Refine = true
  Suppressed = false
  Type = 1
FEATURE [PartDesign::Fillet] Fillet
  Base = -> Pocket [Edge43,Edge37,Edge25,Edge31]
  BaseFeature = -> Pocket
  Placement = pos=(0,0,0) rot=(1,0,0;1.5708rad)
  Radius = 0.1
  Refine = true
  SupportTransform = false
  Suppressed = false
  UseAllEdges = false
FEATURE [PartDesign::AdditiveHelix] AdditiveHelix
  Angle = 0
  Axis = (0,2e-16,1)
  Base = (0,0,0)
  BaseFeature = -> Fillet
  Growth = 0
  HasBeenEdited = true
  Height = 8
  LeftHanded = false
  Mode = 0
  Outside = false
  Pitch = 0.35
  Placement = pos=(0,0,0) rot=(1,0,0;1.5708rad)
  Profile = -> Sketch001
  ReferenceAxis = -> Sketch001 [V_Axis]
  Suppressed = false
  Tolerance = 0.1
  Turns = 22.8571
  expr: Height = <<Profile>>.Constraints.L
FEATURE [PartDesign::CoordinateSystem] LCS_1
  AttacherType = Attacher::AttachEngine3D
FEATURE [PartDesign::Body] Body  label="SCREW-M1.6x8"
  AllowCompound = false
  Group = -> [Sketch,Revolution,Pocket,Fillet,Sketch001,AdditiveHelix,Sketch002,LCS_1]
  Origin = -> Origin
  Tip = -> AdditiveHelix
---- part ../Design/SPACER/SPACER.FCStd = doc fcstd_444523f21eb5 ----
FCSTD DOCUMENT  (FreeCAD 1.0R38641 +678 (Git))
Label: SPACER
License: All rights reserved
LicenseURL: https://en.wikipedia.org/wiki/All_rights_reserved
objects: TechDraw::DrawViewDimension×7, Sketcher::SketchObject×2, TechDraw::DrawProjGroupItem×2, PartDesign::CoordinateSystem×2, TechDraw::DrawSVGTemplate×1, PartDesign::Revolution×1, TechDraw::DrawViewSection×1, TechDraw::DrawProjGroup×1, TechDraw::DrawViewBalloon×1, TechDraw::DrawPage×1, PartDesign::Body×1
note: 23 computed .brp shape members not serialized (recipe doc carries the construction recipe); baked Part::Feature solids carry a one-line shape summary decoded from their .brp

FEATURE [TechDraw::DrawSVGTemplate] Template
  EditableTexts = CreationDate=2026/03/20; E.G.APPROVED=Approved; FC-Scale=5:1; FC-Title=SPACER; IntechStudioLtd.=Intech Studio Ltd.; MATERIAL=brass; REV=04; STANDARD=+/-0,1
  Height = 297
  Orientation = 1
  Template = <userpath>/Documents/grid-hardware/Manufacturing/FreeCAD_technical_drawing_template/A3_LandscapeTD_MODIFIED.svg
  Width = 420
FEATURE [Sketcher::SketchObject] Sketch009
  ArcFitTolerance = 0
  AttachmentSupport = -> [YZ_Plane004]
  FullyConstrained = true
  MakeInternals = false
  MapMode = 5
  Placement = pos=(0,0,0) rot=(0.57735,0.57735,0.57735;2.0944rad)
  sketch-geometry (1):
    g0: LineSegment StartX=0 StartY=9 StartZ=0 EndX=0 EndY=-1 EndZ=0
  constraints (4):
    c: PointOnObject(g0,g-2)
    c: DistanceY(g0,g0) = 10
    c: DistanceY(g0,g-1) = 1
    c: Vertical(g0)
FEATURE [Sketcher::SketchObject] Sketch008
  ArcFitTolerance = 0
  AttachmentSupport = -> [YZ_Plane004]
  FullyConstrained = true
  MakeInternals = false
  MapMode = 5
  Placement = pos=(0,0,0) rot=(0.57735,0.57735,0.57735;2.0944rad)
  expr: Constraints[16] = 3.3 / 2
  expr: Constraints[24] = 5.875 mm
  sketch-geometry (23):
    g0: LineSegment StartX=-1.9 StartY=8.3 StartZ=0 EndX=-3.25 EndY=8.3 EndZ=0
    g1: LineSegment StartX=-1.65 StartY=8.05 StartZ=0 EndX=-1.65 EndY=2 EndZ=0
    g2: LineSegment StartX=-1.65 StartY=2 StartZ=0 EndX=-0.85 EndY=2 EndZ=0
    g3: LineSegment StartX=-0.85 StartY=2 StartZ=0 EndX=-0.85 EndY=0 EndZ=0
    g4: LineSegment StartX=-0.85 StartY=0 StartZ=0 EndX=-5.625 EndY=0 EndZ=0
    g5: LineSegment StartX=-5.625 StartY=0 StartZ=0 EndX=-5.875 EndY=0.25 EndZ=0
    g6: LineSegment StartX=-3.5 StartY=8.05 StartZ=0 EndX=-3.25 EndY=8.3 EndZ=0
    g7: LineSegment StartX=-1.9 StartY=8.3 StartZ=0 EndX=-1.65 EndY=8.05 EndZ=0
    g8: LineSegment StartX=-5.875 StartY=3.35 StartZ=0 EndX=-5.875 EndY=0.25 EndZ=0
    g9: LineSegment StartX=-5.625 StartY=3.6 StartZ=0 EndX=-5.875 EndY=3.35 EndZ=0
    g10: LineSegment StartX=-3.75 StartY=3.6 StartZ=0 EndX=-5.625 EndY=3.6 EndZ=0
    g11: LineSegment StartX=-3.5 StartY=8.05 StartZ=0 EndX=-3.5 EndY=3.85 EndZ=0
    g12: LineSegment StartX=-3.5 StartY=3.85 StartZ=0 EndX=-3.75 EndY=3.6 EndZ=0
    g13: LineSegment [constr] StartX=-3.5 StartY=8.05 StartZ=0 EndX=-3.25 EndY=8.05 EndZ=0
    g14: LineSegment [constr] StartX=-3.25 StartY=8.05 StartZ=0 EndX=-3.25 EndY=8.3 EndZ=0
    g15: LineSegment [constr] StartX=-1.9 StartY=8.3 StartZ=0 EndX=-1.9 EndY=8.05 EndZ=0
    g16: LineSegment [constr] StartX=-1.9 StartY=8.05 StartZ=0 EndX=-1.65 EndY=8.05 EndZ=0
    g17: LineSegment [constr] StartX=-3.75 StartY=3.6 StartZ=0 EndX=-3.5 EndY=3.6 EndZ=0
    g18: LineSegment [constr] StartX=-3.5 StartY=3.6 StartZ=0 EndX=-3.5 EndY=3.85 EndZ=0
    g19: LineSegment [constr] StartX=-5.875 StartY=3.35 StartZ=0 EndX=-5.625 EndY=3.35 EndZ=0
    g20: LineSegment [constr] StartX=-5.625 StartY=3.35 StartZ=0 EndX=-5.625 EndY=3.6 EndZ=0
    g21: LineSegment [constr] StartX=-5.875 StartY=0.25 StartZ=0 EndX=-5.625 EndY=0.25 EndZ=0
    g22: LineSegment [constr] StartX=-5.625 StartY=0.25 StartZ=0 EndX=-5.625 EndY=0 EndZ=0
  constraints (65):
    c: Horizontal(g0)
    c: Coincident(g2,g1)
    c: Horizontal(g2)
    c: Vertical(g1)
    c: Vertical(g3)
    c: Coincident(g2,g3)
    c: DistanceX(g2,g-1) = 0.85
    c: Horizontal(g4)
    c: Coincident(g11,g6)
    c: Coincident(g0,g6)
    c: DistanceY(g11,g0) = 0.25
    c: Coincident(g8,g5)
    c: Coincident(g4,g5)
    c: Angle(g7,g1) = 2.35619
    c: Coincident(g0,g7)
    c: Coincident(g1,g7)
    c: DistanceX(g1,g-1) = 1.65
    c: DistanceY(g-1,g3) = 0
    c: DistanceY(g-1,g2) = 2
    c: DistanceY(g-1,g4) = 0
    c: DistanceY(g-1,g0) = 8.3
    c: Equal(g5,g6)
    c: Equal(g7,g6)
    c: Coincident(g4,g3)
    c: DistanceX(g8,g-1) = 5.875
    c: Coincident(g9,g8)
    c: Vertical(g8)
    c: Coincident(g10,g9)
    c: Coincident(g12,g10)
    c: Coincident(g11,g12)
    c: Vertical(g11)
    c: Horizontal(g10)
    c: Coincident(g6,g13)
    c: Horizontal(g13)
    c: Coincident(g13,g14)
    c: Coincident(g14,g0)
    c: Coincident(g0,g15)
    c: Vertical(g15)
    c: Coincident(g15,g16)
    c: Coincident(g16,g1)
    c: Horizontal(g16)
    c: Vertical(g14)
    c: Equal(g13,g14)
    c: Coincident(g10,g17)
    c: Horizontal(g17)
    c: Coincident(g17,g18)
    c: Coincident(g18,g11)
    c: Vertical(g18)
    c: Coincident(g8,g19)
    c: Horizontal(g19)
    c: Coincident(g19,g20)
    c: Coincident(g20,g9)
    c: Vertical(g20)
    c: Equal(g20,g19)
    c: Equal(g17,g18)
    c: Equal(g12,g9)
    c: Equal(g9,g5)
    c: Coincident(g5,g21)
    c: Coincident(g21,g22)
    c: Coincident(g22,g4)
    c: Vertical(g22)
    c: Horizontal(g21)
    c: Equal(g21,g22)
    c: DistanceY(g4,g9) = 3.6
    c: DistanceX(g11,g-1) = 3.5
FEATURE [PartDesign::Revolution] Revolution
  Angle = 360
  Angle2 = 60
  Axis = (0,0,1)
  Base = (0,0,0)
  Placement = pos=(0,0,0) rot=(1,1,1;2.0944rad)
  Profile = -> Sketch008
  ReferenceAxis = -> Sketch008 [V_Axis]
  Suppressed = false
  Type = 0
FEATURE [TechDraw::DrawProjGroupItem] ProjItem  label="Front"
  CoarseView = false
  Direction = (0,-1,0)
  Focus = 100
  HardHidden = false
  IsoCount = 0
  IsoHidden = false
  IsoVisible = false
  LockPosition = true
  Perspective = false
  Rotation = 0
  RotationVector = (1,0,0)
  Scale = 5
  ScaleType = 2
  ScrubCount = 0
  SeamHidden = false
  SeamVisible = false
  SmoothHidden = false
  SmoothVisible = true
  Source = -> [Revolution]
  Type = 0
  X = 0
  XDirection = (1,0,0)
  Y = 0
FEATURE [TechDraw::DrawViewSection] SectionView  label="Section A - A"
  BaseView = -> ProjItem
  Caption = Section A - A
  CoarseView = false
  CutSurfaceDisplay = 2
  Direction = (-1,0,-1e-16)
  FileGeomPattern = /snap/freecad/1202/usr/share/Mod/TechDraw/PAT/FCPAT.pat
  FileHatchPattern = /snap/freecad/1202/usr/share/Mod/TechDraw/Patterns/simple.svg
  Focus = 100
  FuseBeforeCut = false
  HardHidden = false
  HatchOffset = (0,0,0)
  HatchRotation = 0
  HatchScale = 1
  IsoCount = 0
  IsoHidden = false
  IsoVisible = false
  LockPosition = false
  NameGeomPattern = Diamond
  Perspective = false
  Rotation = -90
  Scale = 5
  ScaleType = 0
  ScrubCount = 0
  SeamHidden = false
  SeamVisible = false
  SectionDirection = 4
  SectionLineStretch = 1
  SectionNormal = (-1,0,-1e-16)
  SectionOrigin = (0,0,4.15)
  SectionSymbol = A
  SmoothHidden = false
  SmoothVisible = true
  Source = -> [Revolution]
  TrimAfterCut = false
  UsePreviousCut = false
  X = 249.527
  XDirection = (1e-16,0,-1)
  Y = 208.158
FEATURE [TechDraw::DrawProjGroupItem] ProjItem001  label="Top"
  CoarseView = false
  Direction = (0,0,1)
  Focus = 100
  HardHidden = false
  IsoCount = 0
  IsoHidden = false
  IsoVisible = false
  LockPosition = false
  Perspective = false
  Rotation = 0
  RotationVector = (1,0,0)
  ScaleType = 2
  ScrubCount = 0
  SeamHidden = false
  SeamVisible = false
  SmoothHidden = false
  SmoothVisible = true
  Source = -> [Revolution]
  Type = 4
  X = 0
  XDirection = (1,0,0)
  Y = -90.125
FEATURE [TechDraw::DrawProjGroup] ProjGroup
  Anchor = -> ProjItem
  AutoDistribute = true
  LockPosition = false
  ProjectionType = 0
  Rotation = 0
  Scale = 5
  ScaleType = 0
  Source = -> [Revolution]
  Views = -> [ProjItem,ProjItem001]
  X = 106.303
  Y = 208.166
  spacingX = 40
  spacingY = 40
FEATURE [TechDraw::DrawViewBalloon] Balloon
  BubbleShape = 1
  EndType = 0
  EndTypeScale = 5
  KinkLength = 5
  LockPosition = false
  OriginX = 4
  OriginY = 4.4
  Rotation = 0
  Scale = 5
  ScaleType = 0
  ShapeScale = 1
  SourceView = -> ProjItem
  Text = Chamfer 0.25mm x 45°
  TextWrapLen = -1
  X = 13.3781
  Y = 6.53229
FEATURE [TechDraw::DrawViewDimension] Dimension002
  AngleOverride = false
  Arbitrary = false
  ArbitraryTolerances = false
  BoxCorners = (2) [(-29.375,-20.75,-1e-07),(29.375,20.75,1e-07)]
  EqualTolerance = true
  ExtensionAngle = 0
  FormatSpec = ⌀%.2w
  FormatSpecOverTolerance = %+.2w
  FormatSpecUnderTolerance = %+.2w
  Inverted = false
  LineAngle = 0
  LockPosition = false
  MeasureType = 1
  OverTolerance = 0
  References2D = -> [SectionView]
  Rotation = 0
  Scale = 5
  ScaleType = 0
  TheoreticalExact = false
  Type = 1
  UnderTolerance = 0
  X = 0
  Y = 35.4315
FEATURE [TechDraw::DrawViewDimension] Dimension003
  AngleOverride = false
  Arbitrary = false
  ArbitraryTolerances = false
  BoxCorners = (2) [(-29.375,-20.75,-1e-07),(29.375,20.75,1e-07)]
  EqualTolerance = false
  ExtensionAngle = 0
  FormatSpec = ⌀%.2w
  FormatSpecOverTolerance = %+.2w
  FormatSpecUnderTolerance = %+.2w
  Inverted = false
  LineAngle = 0
  LockPosition = false
  MeasureType = 1
  OverTolerance = 0.2
  References2D = -> [SectionView]
  Rotation = 0
  Scale = 5
  ScaleType = 0
  TheoreticalExact = false
  Type = 1
  UnderTolerance = 0
  X = 0
  Y = 52.7979
FEATURE [TechDraw::DrawViewDimension] Dimension004
  AngleOverride = false
  Arbitrary = false
  ArbitraryTolerances = false
  BoxCorners = (2) [(-29.375,-20.75,-1e-07),(29.375,20.75,1e-07)]
  EqualTolerance = true
  ExtensionAngle = 0
  FormatSpec = %.2w
  FormatSpecOverTolerance = %+.2w
  FormatSpecUnderTolerance = %+.2w
  Inverted = false
  LineAngle = 0
  LockPosition = false
  MeasureType = 1
  OverTolerance = 0
  References2D = -> [SectionView]
  Rotation = 0
  Scale = 5
  ScaleType = 0
  TheoreticalExact = false
  Type = 2
  UnderTolerance = 0
  X = -49.6071
  Y = -15.75
FEATURE [TechDraw::DrawViewDimension] Dimension005
  AngleOverride = false
  Arbitrary = false
  ArbitraryTolerances = false
  BoxCorners = (2) [(-29.375,-20.75,-1e-07),(29.375,20.75,1e-07)]
  EqualTolerance = true
  ExtensionAngle = 0
  FormatSpec = ⌀%.2w
  FormatSpecOverTolerance = %+.2w
  FormatSpecUnderTolerance = %+.2w
  Inverted = false
  LineAngle = 0
  LockPosition = false
  MeasureType = 1
  OverTolerance = 0
  References2D = -> [SectionView]
  Rotation = 0
  Scale = 5
  ScaleType = 0
  TheoreticalExact = false
  Type = 1
  UnderTolerance = 0
  X = 0
  Y = 71.5638
FEATURE [TechDraw::DrawViewDimension] Dimension
  AngleOverride = false
  Arbitrary = false
  ArbitraryTolerances = false
  BoxCorners = (2) [(-29.375,-29.375,0),(29.375,29.375,0)]
  EqualTolerance = true
  ExtensionAngle = 0
  FormatSpec = ⌀%.2w
  FormatSpecOverTolerance = %+.2w
  FormatSpecUnderTolerance = %+.2w
  Inverted = false
  LineAngle = 0
  LockPosition = false
  MeasureType = 1
  OverTolerance = 0
  References2D = -> [ProjItem001]
  Rotation = 0
  Scale = 5
  ScaleType = 0
  TheoreticalExact = false
  Type = 5
  UnderTolerance = 0
  X = -60.0722
  Y = -17.5385
FEATURE [TechDraw::DrawViewDimension] Dimension006
  AngleOverride = false
  Arbitrary = false
  ArbitraryTolerances = false
  BoxCorners = (2) [(-29.375,-20.75,-1e-07),(29.375,20.75,1e-07)]
  EqualTolerance = false
  ExtensionAngle = 0
  FormatSpec = %.2w
  FormatSpecOverTolerance = %+.2w
  FormatSpecUnderTolerance = %+.2w
  Inverted = false
  LineAngle = 0
  LockPosition = false
  MeasureType = 1
  OverTolerance = 0
  References2D = -> [ProjItem]
  Rotation = 0
  Scale = 5
  ScaleType = 0
  TheoreticalExact = false
  Type = 0
  UnderTolerance = -0.1
  X = -58.7208
  Y = -36.3695
FEATURE [TechDraw::DrawViewDimension] Dimension007
  AngleOverride = false
  Arbitrary = false
  ArbitraryTolerances = false
  BoxCorners = (2) [(-29.375,-20.75,-1e-07),(29.375,20.75,1e-07)]
  EqualTolerance = false
  ExtensionAngle = 0
  FormatSpec = %.2w
  FormatSpecOverTolerance = %+.2w
  FormatSpecUnderTolerance = %+.2w
  Inverted = false
  LineAngle = 0
  LockPosition = false
  MeasureType = 1
  OverTolerance = 0
  References2D = -> [ProjItem]
  Rotation = 0
  Scale = 5
  ScaleType = 0
  TheoreticalExact = false
  Type = 0
  UnderTolerance = -0.1
  X = -39.8312
  Y = -37.1705
FEATURE [TechDraw::DrawPage] Page  label="SPACER_Drawing"
  KeepUpdated = true
  NextBalloonIndex = 2
  ProjectionType = 0
  Scale = 5
  Template = -> Template
  Views = -> [SectionView,ProjGroup,Balloon,Dimension002,Dimension003,Dimension004,Dimension005,Dimension,Dimension006,Dimension007]
FEATURE [PartDesign::CoordinateSystem] LCS_1
  AttacherType = Attacher::AttachEngine3D
FEATURE [PartDesign::CoordinateSystem] LCS_2
  AttacherType = Attacher::AttachEngine3D
  AttachmentSupport = -> [Revolution]
  MapMode = 11
  Placement = pos=(-7e-16,2e-16,2) rot=(0,0,1;0rad)
FEATURE [PartDesign::Body] Body004  label="SPACER"
  AllowCompound = false
  Group = -> [Sketch008,Revolution,Sketch009,LCS_1,LCS_2]
  Origin = -> Origin004
  Tip = -> Revolution
---- part ../Design/THT-HALL-SWITCH/THT-HALL-SWITCH.FCStd = doc fcstd_0d8cac5cee19 ----
FCSTD DOCUMENT  (FreeCAD 1.0R39319 (Git))
Label: THT-HALL-SWITCH
License: All rights reserved
LicenseURL: https://en.wikipedia.org/wiki/All_rights_reserved
objects: PartDesign::CoordinateSystem×2, Part::Feature×1, PartDesign::FeatureBase×1, PartDesign::Body×1
note: 6 computed .brp shape members not serialized (recipe doc carries the construction recipe); baked Part::Feature solids carry a one-line shape summary decoded from their .brp

FEATURE [Part::Feature] Part__Feature  label="SOLID"
  Placement = pos=(13.3,-4.5,-1.1) rot=(0,0,1;0rad)
  shape: bbox 14.78 x 14.78 x 13.28 mm, 728 faces (baked)
FEATURE [PartDesign::CoordinateSystem] LCS_Origin
  AttacherType = Attacher::AttachEngine3D
  AttachmentOffset = pos=(-13.3,4.5,1.1) rot=(0,0,1;0rad)
  AttachmentSupport = -> [X_Axis]
  MapMode = 2
  Placement = pos=(-13.3,4.5,1.1) rot=(0,0,1;0rad)
FEATURE [PartDesign::FeatureBase] BaseFeature
  BaseFeature = -> Part__Feature
  Suppressed = false
FEATURE [PartDesign::CoordinateSystem] LCS_1
  AttacherType = Attacher::AttachEngine3D
  AttachmentSupport = -> [BaseFeature]
  MapMode = 11
  Placement = pos=(-13.3,4.5,8.00025) rot=(0.707107,0.707107,0;3.14159rad)
FEATURE [PartDesign::Body] Body
  AllowCompound = false
  BaseFeature = -> Part__Feature
  Group = -> [BaseFeature,LCS_Origin,LCS_1]
  Origin = -> Origin
  Tip = -> BaseFeature
